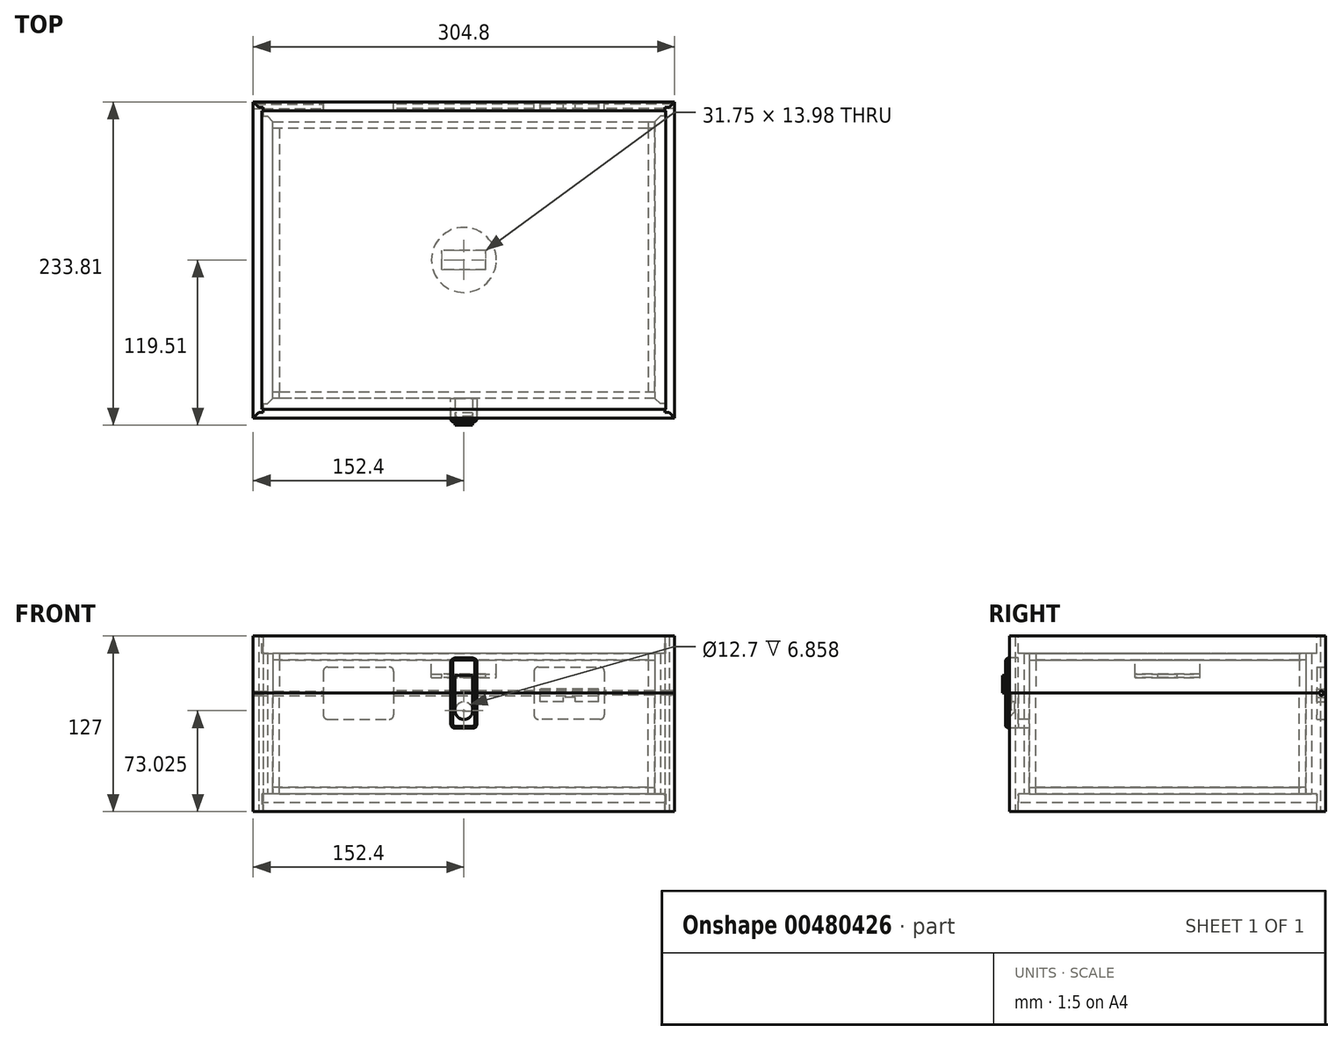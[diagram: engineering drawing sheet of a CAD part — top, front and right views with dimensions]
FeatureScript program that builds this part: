
annotation { "Feature Type Name" : "Feature", "Feature Type Description" : "" }
export const myFeature = defineFeature(function(context is Context, id is Id, definition is map)
    precondition{}
    {
        {
            var Q0;
            Q0=qCreatedBy(makeId("Top.planeOp"),FACE);
            var sketch = newSketch(context, id + "F0", { "sketchPlane" : qUnion([Q0])});
            skLineSegment(sketch, "E0.bottom", {"start": v(152.4, 114.3) * mm, "end": v(-152.4, 114.3) * mm});
            skLineSegment(sketch, "E0.top", {"start": v(152.4, -114.3) * mm, "end": v(-152.4, -114.3) * mm});
            skLineSegment(sketch, "E0.left", {"start": v(152.4, 114.3) * mm, "end": v(152.4, -114.3) * mm});
            skLineSegment(sketch, "E0.right", {"start": v(-152.4, 114.3) * mm, "end": v(-152.4, -114.3) * mm});
            skPoint(sketch, "E0.middle", {"position": v(0, 0) * mm});
            skPoint(sketch, "E1.endSnap0", {"position": v(0, 114.3) * mm});
            skPoint(sketch, "E2.endSnap0", {"position": v(0, -114.3) * mm});
            skPoint(sketch, "E3.endSnap0", {"position": v(-152.4, 0) * mm});
            skLineSegment(sketch, "E4", {"start": v(152.4, 114.3) * mm, "end": v(138.11, 100.01) * mm});
            skLineSegment(sketch, "E5", {"start": v(145.26, 107.16) * mm, "end": v(145.26, 103.98) * mm});
            skLineSegment(sketch, "E6", {"start": v(145.26, 103.98) * mm, "end": v(142.08, 103.98) * mm});
            skLineSegment(sketch, "E7", {"start": v(145.26, 107.16) * mm, "end": v(145.26, 110.33) * mm});
            skLineSegment(sketch, "E8", {"start": v(145.26, 110.33) * mm, "end": v(148.43, 110.33) * mm});
            skLineSegment(sketch, "E9", {"start": v(152.4, -114.3) * mm, "end": v(138.11, -100.01) * mm});
            skLineSegment(sketch, "E10", {"start": v(-152.4, -114.3) * mm, "end": v(-138.11, -100.01) * mm});
            skLineSegment(sketch, "E11", {"start": v(-152.4, 114.3) * mm, "end": v(-138.11, 100.01) * mm});
            skLineSegment(sketch, "E12", {"start": v(145.26, -107.16) * mm, "end": v(145.26, -103.98) * mm});
            skLineSegment(sketch, "E13", {"start": v(145.26, -103.98) * mm, "end": v(142.08, -103.98) * mm});
            skLineSegment(sketch, "E14", {"start": v(145.26, -107.16) * mm, "end": v(145.26, -110.33) * mm});
            skLineSegment(sketch, "E15", {"start": v(145.26, -110.33) * mm, "end": v(148.43, -110.33) * mm});
            skLineSegment(sketch, "E16", {"start": v(-145.26, -107.16) * mm, "end": v(-145.26, -103.98) * mm});
            skLineSegment(sketch, "E17", {"start": v(-145.26, -103.98) * mm, "end": v(-142.08, -103.98) * mm});
            skLineSegment(sketch, "E18", {"start": v(-145.26, -107.16) * mm, "end": v(-145.26, -110.33) * mm});
            skLineSegment(sketch, "E19", {"start": v(-145.26, -110.33) * mm, "end": v(-148.43, -110.33) * mm});
            skLineSegment(sketch, "E20", {"start": v(-145.26, 107.16) * mm, "end": v(-145.26, 103.98) * mm});
            skLineSegment(sketch, "E21", {"start": v(-145.26, 103.98) * mm, "end": v(-142.08, 103.98) * mm});
            skLineSegment(sketch, "E22", {"start": v(-145.26, 107.16) * mm, "end": v(-145.26, 110.33) * mm});
            skLineSegment(sketch, "E23", {"start": v(-145.26, 110.33) * mm, "end": v(-148.43, 110.33) * mm});
            skLineSegment(sketch, "E24", {"start": v(-138.11, 100.01) * mm, "end": v(138.11, 100.01) * mm});
            skLineSegment(sketch, "E25", {"start": v(138.11, 100.01) * mm, "end": v(138.11, -100.01) * mm});
            skLineSegment(sketch, "E26", {"start": v(138.11, -100.01) * mm, "end": v(-138.11, -100.01) * mm});
            skLineSegment(sketch, "E27", {"start": v(-138.11, -100.01) * mm, "end": v(-138.11, 100.01) * mm});
            skSolve(sketch);
        }
        {
            var Q0;
            {var subQ5=sQuery(id+"F0.wireOp",EDGE,"E0.bottom");Q0=makeQuery(id+"F0.imprint","IMPRINT",FACE,{"disambiguationData":[TD([[makeQuery(id+"F0.imprint","IMPRINT",EDGE,{"derivedFrom":subQ5}),1.0]])]});}
            var Q1;
            {var subQ5=sQuery(id+"F0.wireOp",EDGE,"E0.top");Q1=makeQuery(id+"F0.imprint","IMPRINT",FACE,{"disambiguationData":[TD([[makeQuery(id+"F0.imprint","IMPRINT",EDGE,{"derivedFrom":subQ5}),-1.0]])]});}
            var Q2;
            {var subQ0=sQuery(id+"F0.wireOp",EDGE,"E16");Q2=makeQuery(id+"F0.imprint","IMPRINT",FACE,{"disambiguationData":[TD([[makeQuery(id+"F0.imprint","IMPRINT",EDGE,{"derivedFrom":subQ0}),-1.0]])]});}
            var Q3;
            {var subQ0=sQuery(id+"F0.wireOp",EDGE,"E12");Q3=makeQuery(id+"F0.imprint","IMPRINT",FACE,{"disambiguationData":[TD([[makeQuery(id+"F0.imprint","IMPRINT",EDGE,{"derivedFrom":subQ0}),1.0]])]});}
            var Q4;
            {var subQ0=sQuery(id+"F0.wireOp",EDGE,"E5");Q4=makeQuery(id+"F0.imprint","IMPRINT",FACE,{"disambiguationData":[TD([[makeQuery(id+"F0.imprint","IMPRINT",EDGE,{"derivedFrom":subQ0}),-1.0]])]});}
            var Q5;
            {var subQ0=sQuery(id+"F0.wireOp",EDGE,"E20");Q5=makeQuery(id+"F0.imprint","IMPRINT",FACE,{"disambiguationData":[TD([[makeQuery(id+"F0.imprint","IMPRINT",EDGE,{"derivedFrom":subQ0}),1.0]])]});}
            extrude(context, id + "F1", {"entities" : qUnion([Q0, Q1, Q2, Q3, Q4, Q5]), "depth" : 85.72 * mm});
        }
        {
            var Q0;
            {var subQ1=sQuery(id+"F0.wireOp",EDGE,"E0.left");Q0=makeQuery(id+"F0.imprint","IMPRINT",FACE,{"disambiguationData":[TD([[makeQuery(id+"F0.imprint","IMPRINT",EDGE,{"derivedFrom":subQ1}),-1.0]])]});}
            var Q1;
            {var subQ6=sQuery(id+"F0.wireOp",EDGE,"E0.right");Q1=makeQuery(id+"F0.imprint","IMPRINT",FACE,{"disambiguationData":[TD([[makeQuery(id+"F0.imprint","IMPRINT",EDGE,{"derivedFrom":subQ6}),1.0]])]});}
            var Q2;
            {var subQ0=sQuery(id+"F0.wireOp",EDGE,"E22");Q2=makeQuery(id+"F0.imprint","IMPRINT",FACE,{"disambiguationData":[TD([[makeQuery(id+"F0.imprint","IMPRINT",EDGE,{"derivedFrom":subQ0}),1.0]])]});}
            var Q3;
            {var subQ0=sQuery(id+"F0.wireOp",EDGE,"E7");Q3=makeQuery(id+"F0.imprint","IMPRINT",FACE,{"disambiguationData":[TD([[makeQuery(id+"F0.imprint","IMPRINT",EDGE,{"derivedFrom":subQ0}),-1.0]])]});}
            var Q4;
            {var subQ0=sQuery(id+"F0.wireOp",EDGE,"E14");Q4=makeQuery(id+"F0.imprint","IMPRINT",FACE,{"disambiguationData":[TD([[makeQuery(id+"F0.imprint","IMPRINT",EDGE,{"derivedFrom":subQ0}),1.0]])]});}
            var Q5;
            {var subQ0=sQuery(id+"F0.wireOp",EDGE,"E18");Q5=makeQuery(id+"F0.imprint","IMPRINT",FACE,{"disambiguationData":[TD([[makeQuery(id+"F0.imprint","IMPRINT",EDGE,{"derivedFrom":subQ0}),-1.0]])]});}
            extrude(context, id + "F2", {"entities" : qUnion([Q0, Q1, Q2, Q3, Q4, Q5]), "depth" : 85.72 * mm});
        }
        {
            var Q0;
            Q0=makeQuery(id+"F1.opExtrude","CAP_FACE",FACE,{"disambiguationData":[OSD([sQuery(id+"F0.wireOp",EDGE,"E0.top"),sQuery(id+"F0.wireOp",EDGE,"E9"),sQuery(id+"F0.wireOp",EDGE,"E10"),sQuery(id+"F0.wireOp",EDGE,"E12"),sQuery(id+"F0.wireOp",EDGE,"E13"),sQuery(id+"F0.wireOp",EDGE,"E14"),sQuery(id+"F0.wireOp",EDGE,"E15"),sQuery(id+"F0.wireOp",EDGE,"E16"),sQuery(id+"F0.wireOp",EDGE,"E17"),sQuery(id+"F0.wireOp",EDGE,"E18"),sQuery(id+"F0.wireOp",EDGE,"E19"),sQuery(id+"F0.wireOp",EDGE,"E26")])],"isStart":true});
            var sketch = newSketch(context, id + "F3", { "sketchPlane" : qUnion([Q0])});
            skLineSegment(sketch, "E28.bottom", {"start": v(146.05, -107.95) * mm, "end": v(-146.05, -107.95) * mm});
            skLineSegment(sketch, "E28.top", {"start": v(146.05, 107.95) * mm, "end": v(-146.05, 107.95) * mm});
            skLineSegment(sketch, "E28.left", {"start": v(146.05, -107.95) * mm, "end": v(146.05, 107.95) * mm});
            skLineSegment(sketch, "E28.right", {"start": v(-146.05, -107.95) * mm, "end": v(-146.05, 107.95) * mm});
            skPoint(sketch, "E28.middle", {"position": v(0, 0) * mm});
            skLineSegment(sketch, "E29.bottom", {"start": v(138.11, 100.01) * mm, "end": v(-138.11, 100.01) * mm});
            skLineSegment(sketch, "E29.top", {"start": v(138.11, -100.01) * mm, "end": v(-138.11, -100.01) * mm});
            skLineSegment(sketch, "E29.left", {"start": v(138.11, 100.01) * mm, "end": v(138.11, -100.01) * mm});
            skLineSegment(sketch, "E29.right", {"start": v(-138.11, 100.01) * mm, "end": v(-138.11, -100.01) * mm});
            skSolve(sketch);
        }
        {
            var Q0;
            Q0 = qSketchRegion(id + "F3", true);
            extrude(context, id + "F4", {"entities" : qUnion([Q0]), "operationType" : NewBodyOperationType.REMOVE, "oppositeDirection" : true, "depth" : 12.7 * mm});
        }
        {
            var Q0;
            Q0=makeQuery(id+"F3.imprint","IMPRINT",FACE,{"disambiguationData":[TD([[makeQuery(id+"F3.imprint","IMPRINT",EDGE,{"derivedFrom":sQuery(id+"F3.wireOp",EDGE,"E29.bottom")}),-1.0]])]});
            var Q1;
            Q1=makeQuery(id+"F3.imprint","IMPRINT",FACE,{"disambiguationData":[TD([[makeQuery(id+"F3.imprint","IMPRINT",EDGE,{"derivedFrom":sQuery(id+"F3.wireOp",EDGE,"E28.bottom")}),-1.0]])]});
            var Q2;
            Q2=makeQuery(id+"F3.imprint","IMPRINT",FACE,{"disambiguationData":[TD([[makeQuery(id+"F3.imprint","IMPRINT",EDGE,{"derivedFrom":sQuery(id+"F3.wireOp",EDGE,"E29.bottom")}),1.0]])]});
            extrude(context, id + "F5", {"entities" : qUnion([Q0, Q1, Q2]), "oppositeDirection" : true, "depth" : 6.35 * mm});
        }
        {
            var Q0;
            Q0=makeQuery(id+"F5.opExtrude","SWEPT_BODY",BODY,{"disambiguationData":[OSD([sQuery(id+"F3.wireOp",EDGE,"E28.bottom"),sQuery(id+"F3.wireOp",EDGE,"E28.top"),sQuery(id+"F3.wireOp",EDGE,"E28.left"),sQuery(id+"F3.wireOp",EDGE,"E28.right")])]});
            var Q1;
            Q1=makeQuery(id+"F1.opExtrude","SWEPT_EDGE",EDGE,{"disambiguationData":[OSD([sQuery(id+"F0.wireOp",EDGE,"E0.bottom"),sQuery(id+"F0.wireOp",EDGE,"E0.right"),sQuery(id+"F0.wireOp",EDGE,"E11")])]});
            transform(context, id + "F6", {"entities" : qUnion([Q0]), "transformType" : TransformType.TRANSLATION_DISTANCE, "transformDirection" : qUnion([Q1]), "distance" : 6.35 * mm, "oppositeDirection" : true, "makeCopy" : false});
        }
        {
            var Q0;
            Q0=makeQuery(id+"F1.opExtrude","CAP_FACE",FACE,{"disambiguationData":[OSD([sQuery(id+"F0.wireOp",EDGE,"E0.bottom"),sQuery(id+"F0.wireOp",EDGE,"E4"),sQuery(id+"F0.wireOp",EDGE,"E5"),sQuery(id+"F0.wireOp",EDGE,"E6"),sQuery(id+"F0.wireOp",EDGE,"E7"),sQuery(id+"F0.wireOp",EDGE,"E8"),sQuery(id+"F0.wireOp",EDGE,"E11"),sQuery(id+"F0.wireOp",EDGE,"E20"),sQuery(id+"F0.wireOp",EDGE,"E21"),sQuery(id+"F0.wireOp",EDGE,"E22"),sQuery(id+"F0.wireOp",EDGE,"E23"),sQuery(id+"F0.wireOp",EDGE,"E24")])],"isStart":false});
            var Q1;
            Q1=makeQuery(id+"F2.opExtrude","CAP_FACE",FACE,{"disambiguationData":[OSD([sQuery(id+"F0.wireOp",EDGE,"E0.right"),sQuery(id+"F0.wireOp",EDGE,"E10"),sQuery(id+"F0.wireOp",EDGE,"E11"),sQuery(id+"F0.wireOp",EDGE,"E16"),sQuery(id+"F0.wireOp",EDGE,"E17"),sQuery(id+"F0.wireOp",EDGE,"E18"),sQuery(id+"F0.wireOp",EDGE,"E19"),sQuery(id+"F0.wireOp",EDGE,"E20"),sQuery(id+"F0.wireOp",EDGE,"E21"),sQuery(id+"F0.wireOp",EDGE,"E22"),sQuery(id+"F0.wireOp",EDGE,"E23"),sQuery(id+"F0.wireOp",EDGE,"E27")])],"isStart":false});
            var Q2;
            Q2=makeQuery(id+"F1.opExtrude","CAP_FACE",FACE,{"disambiguationData":[OSD([sQuery(id+"F0.wireOp",EDGE,"E0.top"),sQuery(id+"F0.wireOp",EDGE,"E9"),sQuery(id+"F0.wireOp",EDGE,"E10"),sQuery(id+"F0.wireOp",EDGE,"E12"),sQuery(id+"F0.wireOp",EDGE,"E13"),sQuery(id+"F0.wireOp",EDGE,"E14"),sQuery(id+"F0.wireOp",EDGE,"E15"),sQuery(id+"F0.wireOp",EDGE,"E16"),sQuery(id+"F0.wireOp",EDGE,"E17"),sQuery(id+"F0.wireOp",EDGE,"E18"),sQuery(id+"F0.wireOp",EDGE,"E19"),sQuery(id+"F0.wireOp",EDGE,"E26")])],"isStart":false});
            var Q3;
            Q3=makeQuery(id+"F2.opExtrude","CAP_FACE",FACE,{"disambiguationData":[OSD([sQuery(id+"F0.wireOp",EDGE,"E0.left"),sQuery(id+"F0.wireOp",EDGE,"E4"),sQuery(id+"F0.wireOp",EDGE,"E5"),sQuery(id+"F0.wireOp",EDGE,"E6"),sQuery(id+"F0.wireOp",EDGE,"E7"),sQuery(id+"F0.wireOp",EDGE,"E8"),sQuery(id+"F0.wireOp",EDGE,"E9"),sQuery(id+"F0.wireOp",EDGE,"E12"),sQuery(id+"F0.wireOp",EDGE,"E13"),sQuery(id+"F0.wireOp",EDGE,"E14"),sQuery(id+"F0.wireOp",EDGE,"E15"),sQuery(id+"F0.wireOp",EDGE,"E25")])],"isStart":false});
            extrude(context, id + "F7", {"entities" : qUnion([Q0, Q1, Q2, Q3]), "depth" : 41.27 * mm});
        }
        {
            var Q0;
            Q0=makeQuery(id+"F7.opExtrude","CAP_FACE",FACE,{"disambiguationData":[OSD([sQuery(id+"F0.wireOp",EDGE,"E0.left"),sQuery(id+"F0.wireOp",EDGE,"E4"),sQuery(id+"F0.wireOp",EDGE,"E5"),sQuery(id+"F0.wireOp",EDGE,"E6"),sQuery(id+"F0.wireOp",EDGE,"E7"),sQuery(id+"F0.wireOp",EDGE,"E8"),sQuery(id+"F0.wireOp",EDGE,"E9"),sQuery(id+"F0.wireOp",EDGE,"E12"),sQuery(id+"F0.wireOp",EDGE,"E13"),sQuery(id+"F0.wireOp",EDGE,"E14"),sQuery(id+"F0.wireOp",EDGE,"E15"),sQuery(id+"F0.wireOp",EDGE,"E25")])],"isStart":false});
            var sketch = newSketch(context, id + "F8", { "sketchPlane" : qUnion([Q0])});
            skLineSegment(sketch, "E30.bottom", {"start": v(146.05, 107.95) * mm, "end": v(-146.05, 107.95) * mm});
            skLineSegment(sketch, "E30.top", {"start": v(146.05, -107.95) * mm, "end": v(-146.05, -107.95) * mm});
            skLineSegment(sketch, "E30.left", {"start": v(146.05, 107.95) * mm, "end": v(146.05, -107.95) * mm});
            skLineSegment(sketch, "E30.right", {"start": v(-146.05, 107.95) * mm, "end": v(-146.05, -107.95) * mm});
            skPoint(sketch, "E30.middle", {"position": v(0, 0) * mm});
            skSolve(sketch);
        }
        {
            var Q0;
            Q0 = qSketchRegion(id + "F8", true);
            extrude(context, id + "F9", {"entities" : qUnion([Q0]), "operationType" : NewBodyOperationType.REMOVE, "oppositeDirection" : true, "depth" : 12.7 * mm});
        }
        {
            var Q0;
            Q0 = qSketchRegion(id + "F8", true);
            extrude(context, id + "F10", {"entities" : qUnion([Q0]), "oppositeDirection" : true, "depth" : 12.7 * mm});
        }
        {
            var Q0;
            Q0=makeQuery(id+"F1.opExtrude","CAP_FACE",FACE,{"disambiguationData":[OSD([sQuery(id+"F0.wireOp",EDGE,"E0.top"),sQuery(id+"F0.wireOp",EDGE,"E9"),sQuery(id+"F0.wireOp",EDGE,"E10"),sQuery(id+"F0.wireOp",EDGE,"E12"),sQuery(id+"F0.wireOp",EDGE,"E13"),sQuery(id+"F0.wireOp",EDGE,"E14"),sQuery(id+"F0.wireOp",EDGE,"E15"),sQuery(id+"F0.wireOp",EDGE,"E16"),sQuery(id+"F0.wireOp",EDGE,"E17"),sQuery(id+"F0.wireOp",EDGE,"E18"),sQuery(id+"F0.wireOp",EDGE,"E19"),sQuery(id+"F0.wireOp",EDGE,"E26")])],"isStart":false});
            var sketch = newSketch(context, id + "F11", { "sketchPlane" : qUnion([Q0])});
            skLineSegment(sketch, "E31.bottom", {"start": v(-138.11, -100.01) * mm, "end": v(138.11, -100.01) * mm});
            skLineSegment(sketch, "E31.top", {"start": v(-138.11, 100.01) * mm, "end": v(138.11, 100.01) * mm});
            skLineSegment(sketch, "E31.left", {"start": v(-138.11, -100.01) * mm, "end": v(-138.11, 100.01) * mm});
            skLineSegment(sketch, "E31.right", {"start": v(138.11, -100.01) * mm, "end": v(138.11, 100.01) * mm});
            skLineSegment(sketch, "E32.bottom", {"start": v(138.11, 100.01) * mm, "end": v(133.35, 100.01) * mm});
            skLineSegment(sketch, "E32.top", {"start": v(138.11, 95.25) * mm, "end": v(133.35, 95.25) * mm});
            skLineSegment(sketch, "E32.left", {"start": v(138.11, 100.01) * mm, "end": v(138.11, 95.25) * mm});
            skLineSegment(sketch, "E32.right", {"start": v(133.35, 100.01) * mm, "end": v(133.35, 95.25) * mm});
            skLineSegment(sketch, "E33.bottom", {"start": v(-138.11, -100.01) * mm, "end": v(-133.35, -100.01) * mm});
            skLineSegment(sketch, "E33.top", {"start": v(-138.11, -95.25) * mm, "end": v(-133.35, -95.25) * mm});
            skLineSegment(sketch, "E33.left", {"start": v(-138.11, -100.01) * mm, "end": v(-138.11, -95.25) * mm});
            skLineSegment(sketch, "E33.right", {"start": v(-133.35, -100.01) * mm, "end": v(-133.35, -95.25) * mm});
            skLineSegment(sketch, "E34.bottom", {"start": v(133.35, 95.25) * mm, "end": v(-133.35, 95.25) * mm});
            skLineSegment(sketch, "E34.top", {"start": v(133.35, -95.25) * mm, "end": v(-133.35, -95.25) * mm});
            skLineSegment(sketch, "E34.left", {"start": v(133.35, 95.25) * mm, "end": v(133.35, -95.25) * mm});
            skLineSegment(sketch, "E34.right", {"start": v(-133.35, 95.25) * mm, "end": v(-133.35, -95.25) * mm});
            skLineSegment(sketch, "E35", {"start": v(-133.35, 95.25) * mm, "end": v(-138.11, 95.25) * mm});
            skLineSegment(sketch, "E36", {"start": v(133.35, -95.25) * mm, "end": v(138.11, -95.25) * mm});
            skSolve(sketch);
        }
        {
            var Q0;
            Q0=makeQuery(id+"F11.imprint","IMPRINT",FACE,{"disambiguationData":[TD([[makeQuery(id+"F11.imprint","IMPRINT",EDGE,{"derivedFrom":sQuery(id+"F11.wireOp",EDGE,"E32.bottom")}),1.0]])]});
            var Q1;
            {var subQ1=sQuery(id+"F11.wireOp",EDGE,"E31.top");Q1=makeQuery(id+"F11.imprint","IMPRINT",FACE,{"disambiguationData":[TD([[makeQuery(id+"F11.imprint","IMPRINT",EDGE,{"derivedFrom":subQ1}),-1.0]])]});}
            var Q2;
            Q2=makeQuery(id+"F11.imprint","IMPRINT",FACE,{"disambiguationData":[TD([[makeQuery(id+"F11.imprint","IMPRINT",EDGE,{"derivedFrom":sQuery(id+"F11.wireOp",EDGE,"E33.bottom")}),-1.0]])]});
            var Q3;
            {var subQ1=sQuery(id+"F11.wireOp",EDGE,"E31.bottom");Q3=makeQuery(id+"F11.imprint","IMPRINT",FACE,{"disambiguationData":[TD([[makeQuery(id+"F11.imprint","IMPRINT",EDGE,{"derivedFrom":subQ1}),-1.0]])]});}
            extrude(context, id + "F12", {"entities" : qUnion([Q0, Q1, Q2, Q3]), "oppositeDirection" : true, "depth" : 68.26 * mm, "hasSecondDirection" : true, "secondDirectionOppositeDirection" : false, "secondDirectionDepth" : 3 / 406.4 * mm});
        }
        {
            var Q0;
            {var subQ0=sQuery(id+"F11.wireOp",EDGE,"E32.top");Q0=makeQuery(id+"F11.imprint","IMPRINT",FACE,{"disambiguationData":[TD([[makeQuery(id+"F11.imprint","IMPRINT",EDGE,{"derivedFrom":subQ0}),1.0]])]});}
            var Q1;
            {var subQ1=sQuery(id+"F11.wireOp",EDGE,"E31.bottom");Q1=makeQuery(id+"F11.imprint","IMPRINT",FACE,{"disambiguationData":[TD([[makeQuery(id+"F11.imprint","IMPRINT",EDGE,{"derivedFrom":subQ1}),-1.0]])]});}
            var Q2;
            Q2=makeQuery(id+"F11.imprint","IMPRINT",FACE,{"disambiguationData":[TD([[makeQuery(id+"F11.imprint","IMPRINT",EDGE,{"derivedFrom":sQuery(id+"F11.wireOp",EDGE,"E34.bottom")}),1.0]])]});
            var Q3;
            Q3=makeQuery(id+"F11.imprint","IMPRINT",FACE,{"disambiguationData":[TD([[makeQuery(id+"F11.imprint","IMPRINT",EDGE,{"derivedFrom":sQuery(id+"F11.wireOp",EDGE,"E32.bottom")}),1.0]])]});
            var Q4;
            {var subQ1=sQuery(id+"F11.wireOp",EDGE,"E31.top");Q4=makeQuery(id+"F11.imprint","IMPRINT",FACE,{"disambiguationData":[TD([[makeQuery(id+"F11.imprint","IMPRINT",EDGE,{"derivedFrom":subQ1}),-1.0]])]});}
            var Q5;
            Q5=makeQuery(id+"F11.imprint","IMPRINT",FACE,{"disambiguationData":[TD([[makeQuery(id+"F11.imprint","IMPRINT",EDGE,{"derivedFrom":sQuery(id+"F11.wireOp",EDGE,"E33.bottom")}),-1.0]])]});
            var Q6;
            {var subQ0=sQuery(id+"F11.wireOp",EDGE,"E33.top");Q6=makeQuery(id+"F11.imprint","IMPRINT",FACE,{"disambiguationData":[TD([[makeQuery(id+"F11.imprint","IMPRINT",EDGE,{"derivedFrom":subQ0}),1.0]])]});}
            extrude(context, id + "F13", {"entities" : qUnion([Q0, Q1, Q2, Q3, Q4, Q5, Q6]), "oppositeDirection" : true, "depth" : 73.02 * mm, "hasSecondDirection" : true, "secondDirectionOppositeDirection" : true, "secondDirectionDepth" : 68.26 * mm});
        }
        {
            var Q0;
            {var subQ0=sQuery(id+"F11.wireOp",EDGE,"E32.top");Q0=makeQuery(id+"F11.imprint","IMPRINT",FACE,{"disambiguationData":[TD([[makeQuery(id+"F11.imprint","IMPRINT",EDGE,{"derivedFrom":subQ0}),1.0]])]});}
            var Q1;
            {var subQ0=sQuery(id+"F11.wireOp",EDGE,"E33.top");Q1=makeQuery(id+"F11.imprint","IMPRINT",FACE,{"disambiguationData":[TD([[makeQuery(id+"F11.imprint","IMPRINT",EDGE,{"derivedFrom":subQ0}),1.0]])]});}
            extrude(context, id + "F14", {"entities" : qUnion([Q0, Q1]), "oppositeDirection" : true, "depth" : 68.26 * mm, "hasSecondDirection" : true, "secondDirectionOppositeDirection" : false, "secondDirectionDepth" : 3 / 406.4 * mm});
        }
        {
            var Q0;
            {var subQ1=sQuery(id+"F11.wireOp",EDGE,"E31.bottom");Q0=makeQuery(id+"F11.imprint","IMPRINT",FACE,{"disambiguationData":[TD([[makeQuery(id+"F11.imprint","IMPRINT",EDGE,{"derivedFrom":subQ1}),-1.0]])]});}
            var Q1;
            Q1=makeQuery(id+"F11.imprint","IMPRINT",FACE,{"disambiguationData":[TD([[makeQuery(id+"F11.imprint","IMPRINT",EDGE,{"derivedFrom":sQuery(id+"F11.wireOp",EDGE,"E33.bottom")}),-1.0]])]});
            var Q2;
            Q2=makeQuery(id+"F11.imprint","IMPRINT",FACE,{"disambiguationData":[TD([[makeQuery(id+"F11.imprint","IMPRINT",EDGE,{"derivedFrom":sQuery(id+"F11.wireOp",EDGE,"E32.bottom")}),1.0]])]});
            var Q3;
            {var subQ1=sQuery(id+"F11.wireOp",EDGE,"E31.top");Q3=makeQuery(id+"F11.imprint","IMPRINT",FACE,{"disambiguationData":[TD([[makeQuery(id+"F11.imprint","IMPRINT",EDGE,{"derivedFrom":subQ1}),-1.0]])]});}
            extrude(context, id + "F15", {"entities" : qUnion([Q0, Q1, Q2, Q3]), "depth" : 23.8 * mm, "hasSecondDirection" : true, "secondDirectionOppositeDirection" : false, "secondDirectionDepth" : 3 / 406.4 * mm});
        }
        {
            var Q0;
            {var subQ1=sQuery(id+"F11.wireOp",EDGE,"E31.bottom");Q0=makeQuery(id+"F11.imprint","IMPRINT",FACE,{"disambiguationData":[TD([[makeQuery(id+"F11.imprint","IMPRINT",EDGE,{"derivedFrom":subQ1}),-1.0]])]});}
            var Q1;
            {var subQ0=sQuery(id+"F11.wireOp",EDGE,"E32.top");Q1=makeQuery(id+"F11.imprint","IMPRINT",FACE,{"disambiguationData":[TD([[makeQuery(id+"F11.imprint","IMPRINT",EDGE,{"derivedFrom":subQ0}),1.0]])]});}
            var Q2;
            Q2=makeQuery(id+"F11.imprint","IMPRINT",FACE,{"disambiguationData":[TD([[makeQuery(id+"F11.imprint","IMPRINT",EDGE,{"derivedFrom":sQuery(id+"F11.wireOp",EDGE,"E34.bottom")}),1.0]])]});
            var Q3;
            Q3=makeQuery(id+"F11.imprint","IMPRINT",FACE,{"disambiguationData":[TD([[makeQuery(id+"F11.imprint","IMPRINT",EDGE,{"derivedFrom":sQuery(id+"F11.wireOp",EDGE,"E32.bottom")}),1.0]])]});
            var Q4;
            {var subQ1=sQuery(id+"F11.wireOp",EDGE,"E31.top");Q4=makeQuery(id+"F11.imprint","IMPRINT",FACE,{"disambiguationData":[TD([[makeQuery(id+"F11.imprint","IMPRINT",EDGE,{"derivedFrom":subQ1}),-1.0]])]});}
            var Q5;
            {var subQ0=sQuery(id+"F11.wireOp",EDGE,"E33.top");Q5=makeQuery(id+"F11.imprint","IMPRINT",FACE,{"disambiguationData":[TD([[makeQuery(id+"F11.imprint","IMPRINT",EDGE,{"derivedFrom":subQ0}),1.0]])]});}
            var Q6;
            Q6=makeQuery(id+"F11.imprint","IMPRINT",FACE,{"disambiguationData":[TD([[makeQuery(id+"F11.imprint","IMPRINT",EDGE,{"derivedFrom":sQuery(id+"F11.wireOp",EDGE,"E33.bottom")}),-1.0]])]});
            extrude(context, id + "F16", {"entities" : qUnion([Q0, Q1, Q2, Q3, Q4, Q5, Q6]), "depth" : 28.57 * mm, "hasSecondDirection" : true, "secondDirectionOppositeDirection" : false, "secondDirectionDepth" : 23.8 * mm});
        }
        {
            var Q0;
            {var subQ0=sQuery(id+"F11.wireOp",EDGE,"E33.top");Q0=makeQuery(id+"F11.imprint","IMPRINT",FACE,{"disambiguationData":[TD([[makeQuery(id+"F11.imprint","IMPRINT",EDGE,{"derivedFrom":subQ0}),1.0]])]});}
            var Q1;
            {var subQ0=sQuery(id+"F11.wireOp",EDGE,"E32.top");Q1=makeQuery(id+"F11.imprint","IMPRINT",FACE,{"disambiguationData":[TD([[makeQuery(id+"F11.imprint","IMPRINT",EDGE,{"derivedFrom":subQ0}),1.0]])]});}
            extrude(context, id + "F17", {"entities" : qUnion([Q0, Q1]), "depth" : 23.8 * mm, "hasSecondDirection" : true, "secondDirectionOppositeDirection" : false, "secondDirectionDepth" : 3 / 406.4 * mm});
        }
        {
            var Q0;
            Q0=makeQuery(id+"F1.opExtrude","SWEPT_FACE",FACE,{"disambiguationData":[OSD([sQuery(id+"F0.wireOp",EDGE,"E0.bottom")])]});
            var sketch = newSketch(context, id + "F18", { "sketchPlane" : qUnion([Q0])});
            skLineSegment(sketch, "E37", {"start": v(-152.4, 85.73) * mm, "end": v(-101.6, 85.73) * mm});
            skLineSegment(sketch, "E38", {"start": v(152.4, 85.73) * mm, "end": v(101.6, 85.73) * mm});
            skLineSegment(sketch, "E39.bottom", {"start": v(-101.6, 85.73) * mm, "end": v(-50.8, 85.73) * mm});
            skLineSegment(sketch, "E39.top", {"start": v(-101.6, 66.8) * mm, "end": v(-50.8, 66.8) * mm});
            skLineSegment(sketch, "E39.left", {"start": v(-101.6, 85.73) * mm, "end": v(-101.6, 66.8) * mm});
            skLineSegment(sketch, "E39.right", {"start": v(-50.8, 85.73) * mm, "end": v(-50.8, 66.8) * mm});
            skLineSegment(sketch, "E40.bottom", {"start": v(101.6, 85.73) * mm, "end": v(50.8, 85.73) * mm});
            skLineSegment(sketch, "E40.top", {"start": v(101.6, 66.8) * mm, "end": v(50.8, 66.8) * mm});
            skLineSegment(sketch, "E40.left", {"start": v(101.6, 85.73) * mm, "end": v(101.6, 66.8) * mm});
            skLineSegment(sketch, "E40.right", {"start": v(50.8, 85.73) * mm, "end": v(50.8, 66.8) * mm});
            skLineSegment(sketch, "E41.top", {"start": v(101.6, 104.65) * mm, "end": v(50.8, 104.65) * mm});
            skLineSegment(sketch, "E41.left", {"start": v(101.6, 85.73) * mm, "end": v(101.6, 104.65) * mm});
            skLineSegment(sketch, "E41.right", {"start": v(50.8, 85.73) * mm, "end": v(50.8, 104.65) * mm});
            skLineSegment(sketch, "E42.bottom", {"start": v(-50.8, 85.73) * mm, "end": v(-101.6, 85.73) * mm});
            skLineSegment(sketch, "E42.top", {"start": v(-50.8, 104.65) * mm, "end": v(-101.6, 104.65) * mm});
            skLineSegment(sketch, "E42.left", {"start": v(-50.8, 85.73) * mm, "end": v(-50.8, 104.65) * mm});
            skLineSegment(sketch, "E42.right", {"start": v(-101.6, 85.73) * mm, "end": v(-101.6, 104.65) * mm});
            skLineSegment(sketch, "E43", {"start": v(-101.6, 85.73) * mm, "end": v(-101.6, 79.38) * mm});
            skLineSegment(sketch, "E44.bottom", {"start": v(-101.6, 79.38) * mm, "end": v(-50.8, 79.38) * mm});
            skLineSegment(sketch, "E44.top", {"start": v(-101.6, 92.08) * mm, "end": v(-50.8, 92.08) * mm});
            skLineSegment(sketch, "E44.left", {"start": v(-101.6, 79.38) * mm, "end": v(-101.6, 92.08) * mm});
            skLineSegment(sketch, "E44.right", {"start": v(-50.8, 79.38) * mm, "end": v(-50.8, 92.08) * mm});
            skLineSegment(sketch, "E45", {"start": v(50.8, 85.73) * mm, "end": v(50.8, 79.38) * mm});
            skLineSegment(sketch, "E46.bottom", {"start": v(50.8, 79.38) * mm, "end": v(101.6, 79.38) * mm});
            skLineSegment(sketch, "E46.top", {"start": v(50.8, 92.08) * mm, "end": v(101.6, 92.08) * mm});
            skLineSegment(sketch, "E46.left", {"start": v(50.8, 79.38) * mm, "end": v(50.8, 92.08) * mm});
            skLineSegment(sketch, "E46.right", {"start": v(101.6, 79.38) * mm, "end": v(101.6, 92.08) * mm});
            skLineSegment(sketch, "E47", {"start": v(-50.8, 79.38) * mm, "end": v(-55.03, 79.38) * mm});
            skLineSegment(sketch, "E48", {"start": v(-55.03, 79.38) * mm, "end": v(-63.5, 79.38) * mm});
            skLineSegment(sketch, "E49", {"start": v(-63.5, 79.38) * mm, "end": v(-76.2, 79.38) * mm});
            skLineSegment(sketch, "E50", {"start": v(-63.5, 79.38) * mm, "end": v(-71.97, 79.38) * mm});
            skLineSegment(sketch, "E51", {"start": v(-71.97, 79.38) * mm, "end": v(-80.43, 79.38) * mm});
            skLineSegment(sketch, "E52", {"start": v(-80.43, 79.38) * mm, "end": v(-88.9, 79.38) * mm});
            skLineSegment(sketch, "E53", {"start": v(-88.9, 79.38) * mm, "end": v(-97.37, 79.38) * mm});
            skLineSegment(sketch, "E54", {"start": v(-97.37, 79.38) * mm, "end": v(-97.37, 92.08) * mm});
            skLineSegment(sketch, "E55", {"start": v(-88.9, 79.38) * mm, "end": v(-88.9, 92.08) * mm});
            skLineSegment(sketch, "E56", {"start": v(-80.43, 79.38) * mm, "end": v(-80.43, 92.08) * mm});
            skLineSegment(sketch, "E57", {"start": v(-71.97, 79.38) * mm, "end": v(-71.97, 92.08) * mm});
            skLineSegment(sketch, "E58", {"start": v(-55.03, 79.38) * mm, "end": v(-55.03, 92.08) * mm});
            skLineSegment(sketch, "E59", {"start": v(-63.5, 79.38) * mm, "end": v(-63.5, 92.08) * mm});
            skLineSegment(sketch, "E60", {"start": v(-101.6, 88.84) * mm, "end": v(-50.8, 88.84) * mm});
            skLineSegment(sketch, "E61", {"start": v(-101.6, 82.55) * mm, "end": v(-50.8, 82.55) * mm});
            skLineSegment(sketch, "E62", {"start": v(50.8, 85.73) * mm, "end": v(55.03, 85.73) * mm});
            skLineSegment(sketch, "E63", {"start": v(55.03, 85.73) * mm, "end": v(63.5, 85.73) * mm});
            skLineSegment(sketch, "E64", {"start": v(63.5, 85.73) * mm, "end": v(71.97, 85.73) * mm});
            skLineSegment(sketch, "E65", {"start": v(71.97, 85.73) * mm, "end": v(80.43, 85.73) * mm});
            skLineSegment(sketch, "E66", {"start": v(80.43, 85.73) * mm, "end": v(88.9, 85.73) * mm});
            skLineSegment(sketch, "E67", {"start": v(88.9, 85.73) * mm, "end": v(97.37, 85.73) * mm});
            skLineSegment(sketch, "E68", {"start": v(55.03, 79.38) * mm, "end": v(55.03, 92.08) * mm});
            skLineSegment(sketch, "E69", {"start": v(63.5, 79.38) * mm, "end": v(63.5, 92.08) * mm});
            skLineSegment(sketch, "E70", {"start": v(71.97, 79.38) * mm, "end": v(71.97, 92.08) * mm});
            skLineSegment(sketch, "E71", {"start": v(80.43, 79.38) * mm, "end": v(80.43, 92.08) * mm});
            skLineSegment(sketch, "E72", {"start": v(88.9, 79.38) * mm, "end": v(88.9, 92.08) * mm});
            skLineSegment(sketch, "E73", {"start": v(97.37, 79.38) * mm, "end": v(97.37, 92.08) * mm});
            skLineSegment(sketch, "E74", {"start": v(50.8, 82.55) * mm, "end": v(101.6, 82.55) * mm});
            skLineSegment(sketch, "E75", {"start": v(50.8, 85.73) * mm, "end": v(50.8, 92.08) * mm});
            skLineSegment(sketch, "E76", {"start": v(50.8, 88.9) * mm, "end": v(101.6, 88.9) * mm});
            skSolve(sketch);
        }
        {
            var Q0;
            Q0=makeQuery(id+"F18.imprint","IMPRINT",FACE,{"disambiguationData":[TD([[makeQuery(id+"F18.imprint","IMPRINT",EDGE,{"derivedFrom":sQuery(id+"F18.wireOp",EDGE,"E39.top")}),1.0]])]});
            var Q1;
            {var subQ0=sQuery(id+"F18.wireOp",EDGE,"E44.bottom");Q1=makeQuery(id+"F18.imprint","IMPRINT",FACE,{"disambiguationData":[TD([[makeQuery(id+"F18.imprint","IMPRINT",EDGE,{"derivedFrom":subQ0}),1.0]])]});}
            var Q2;
            {var subQ1=sQuery(id+"F18.wireOp",EDGE,"E42.bottom");var subQ3=sQuery(id+"F18.wireOp",EDGE,"E54");var subQ4=makeQuery(id+"F18.imprint","INTERSECT",VERTEX,{"derivedFrom":[subQ1,subQ3]});Q2=makeQuery(id+"F18.imprint","IMPRINT",FACE,{"disambiguationData":[TD([[makeQuery(id+"F18.imprint","IMPRINT",EDGE,{"disambiguationData":[TD([[subQ4,1.0]])],"derivedFrom":subQ3}),1.0]])]});}
            var Q3;
            {var subQ1=sQuery(id+"F18.wireOp",EDGE,"E42.bottom");var subQ3=sQuery(id+"F18.wireOp",EDGE,"E54");var subQ4=makeQuery(id+"F18.imprint","INTERSECT",VERTEX,{"derivedFrom":[subQ1,subQ3]});Q3=makeQuery(id+"F18.imprint","IMPRINT",FACE,{"disambiguationData":[TD([[makeQuery(id+"F18.imprint","IMPRINT",EDGE,{"disambiguationData":[TD([[subQ4,-1.0]])],"derivedFrom":subQ3}),1.0]])]});}
            var Q4;
            {var subQ0=sQuery(id+"F18.wireOp",EDGE,"E53");Q4=makeQuery(id+"F18.imprint","IMPRINT",FACE,{"disambiguationData":[TD([[makeQuery(id+"F18.imprint","IMPRINT",EDGE,{"derivedFrom":subQ0}),-1.0]])]});}
            var Q5;
            {var subQ0=sQuery(id+"F18.wireOp",EDGE,"E52");Q5=makeQuery(id+"F18.imprint","IMPRINT",FACE,{"disambiguationData":[TD([[makeQuery(id+"F18.imprint","IMPRINT",EDGE,{"derivedFrom":subQ0}),-1.0]])]});}
            var Q6;
            {var subQ0=sQuery(id+"F18.wireOp",EDGE,"E55");var subQ1=sQuery(id+"F18.wireOp",EDGE,"E42.bottom");var subQ2=makeQuery(id+"F18.imprint","INTERSECT",VERTEX,{"derivedFrom":[subQ1,subQ0]});Q6=makeQuery(id+"F18.imprint","IMPRINT",FACE,{"disambiguationData":[TD([[makeQuery(id+"F18.imprint","IMPRINT",EDGE,{"disambiguationData":[TD([[subQ2,-1.0]])],"derivedFrom":subQ1}),1.0]])]});}
            var Q7;
            {var subQ0=sQuery(id+"F18.wireOp",EDGE,"E55");var subQ1=sQuery(id+"F18.wireOp",EDGE,"E42.bottom");var subQ2=makeQuery(id+"F18.imprint","INTERSECT",VERTEX,{"derivedFrom":[subQ1,subQ0]});Q7=makeQuery(id+"F18.imprint","IMPRINT",FACE,{"disambiguationData":[TD([[makeQuery(id+"F18.imprint","IMPRINT",EDGE,{"disambiguationData":[TD([[subQ2,-1.0]])],"derivedFrom":subQ1}),-1.0]])]});}
            var Q8;
            {var subQ1=sQuery(id+"F18.wireOp",EDGE,"E51");var subQ5=makeQuery(id+"F18.imprint","IMPRINT",VERTEX,{"derivedFrom":subQ1});Q8=makeQuery(id+"F18.imprint","IMPRINT",FACE,{"disambiguationData":[TD([[makeQuery(id+"F18.imprint","IMPRINT",EDGE,{"disambiguationData":[TD([[subQ5,1.0]])],"derivedFrom":subQ1}),-1.0]])]});}
            var Q9;
            {var subQ0=sQuery(id+"F18.wireOp",EDGE,"E50");Q9=makeQuery(id+"F18.imprint","IMPRINT",FACE,{"disambiguationData":[TD([[makeQuery(id+"F18.imprint","IMPRINT",EDGE,{"derivedFrom":subQ0}),-1.0]])]});}
            var Q10;
            {var subQ0=sQuery(id+"F18.wireOp",EDGE,"E48");Q10=makeQuery(id+"F18.imprint","IMPRINT",FACE,{"disambiguationData":[TD([[makeQuery(id+"F18.imprint","IMPRINT",EDGE,{"derivedFrom":subQ0}),-1.0]])]});}
            var Q11;
            {var subQ0=sQuery(id+"F18.wireOp",EDGE,"E57");var subQ1=sQuery(id+"F18.wireOp",EDGE,"E42.bottom");var subQ2=makeQuery(id+"F18.imprint","INTERSECT",VERTEX,{"derivedFrom":[subQ1,subQ0]});Q11=makeQuery(id+"F18.imprint","IMPRINT",FACE,{"disambiguationData":[TD([[makeQuery(id+"F18.imprint","IMPRINT",EDGE,{"disambiguationData":[TD([[subQ2,-1.0]])],"derivedFrom":subQ1}),-1.0]])]});}
            var Q12;
            {var subQ0=sQuery(id+"F18.wireOp",EDGE,"E57");var subQ1=sQuery(id+"F18.wireOp",EDGE,"E42.bottom");var subQ2=makeQuery(id+"F18.imprint","INTERSECT",VERTEX,{"derivedFrom":[subQ1,subQ0]});Q12=makeQuery(id+"F18.imprint","IMPRINT",FACE,{"disambiguationData":[TD([[makeQuery(id+"F18.imprint","IMPRINT",EDGE,{"disambiguationData":[TD([[subQ2,-1.0]])],"derivedFrom":subQ1}),1.0]])]});}
            var Q13;
            {var subQ0=sQuery(id+"F18.wireOp",EDGE,"E47");Q13=makeQuery(id+"F18.imprint","IMPRINT",FACE,{"disambiguationData":[TD([[makeQuery(id+"F18.imprint","IMPRINT",EDGE,{"derivedFrom":subQ0}),-1.0]])]});}
            var Q14;
            {var subQ1=sQuery(id+"F18.wireOp",EDGE,"E42.bottom");var subQ3=sQuery(id+"F18.wireOp",EDGE,"E58");var subQ4=makeQuery(id+"F18.imprint","INTERSECT",VERTEX,{"derivedFrom":[subQ1,subQ3]});Q14=makeQuery(id+"F18.imprint","IMPRINT",FACE,{"disambiguationData":[TD([[makeQuery(id+"F18.imprint","IMPRINT",EDGE,{"disambiguationData":[TD([[subQ4,1.0]])],"derivedFrom":subQ3}),-1.0]])]});}
            var Q15;
            {var subQ1=sQuery(id+"F18.wireOp",EDGE,"E42.bottom");var subQ3=sQuery(id+"F18.wireOp",EDGE,"E58");var subQ4=makeQuery(id+"F18.imprint","INTERSECT",VERTEX,{"derivedFrom":[subQ1,subQ3]});Q15=makeQuery(id+"F18.imprint","IMPRINT",FACE,{"disambiguationData":[TD([[makeQuery(id+"F18.imprint","IMPRINT",EDGE,{"disambiguationData":[TD([[subQ4,-1.0]])],"derivedFrom":subQ3}),-1.0]])]});}
            var Q16;
            {var subQ1=sQuery(id+"F18.wireOp",EDGE,"E46.bottom");var subQ3=sQuery(id+"F18.wireOp",EDGE,"E73");var subQ4=makeQuery(id+"F18.imprint","INTERSECT",VERTEX,{"derivedFrom":[subQ1,subQ3]});Q16=makeQuery(id+"F18.imprint","IMPRINT",FACE,{"disambiguationData":[TD([[makeQuery(id+"F18.imprint","IMPRINT",EDGE,{"disambiguationData":[TD([[subQ4,-1.0]])],"derivedFrom":subQ3}),-1.0]])]});}
            var Q17;
            {var subQ0=sQuery(id+"F18.wireOp",EDGE,"E40.bottom");Q17=makeQuery(id+"F18.imprint","IMPRINT",FACE,{"disambiguationData":[TD([[makeQuery(id+"F18.imprint","IMPRINT",EDGE,{"derivedFrom":subQ0}),-1.0]])]});}
            var Q18;
            {var subQ0=sQuery(id+"F18.wireOp",EDGE,"E40.bottom");Q18=makeQuery(id+"F18.imprint","IMPRINT",FACE,{"disambiguationData":[TD([[makeQuery(id+"F18.imprint","IMPRINT",EDGE,{"derivedFrom":subQ0}),1.0]])]});}
            var Q19;
            {var subQ0=sQuery(id+"F18.wireOp",EDGE,"E62");Q19=makeQuery(id+"F18.imprint","IMPRINT",FACE,{"disambiguationData":[TD([[makeQuery(id+"F18.imprint","IMPRINT",EDGE,{"derivedFrom":subQ0}),1.0]])]});}
            var Q20;
            {var subQ0=sQuery(id+"F18.wireOp",EDGE,"E62");Q20=makeQuery(id+"F18.imprint","IMPRINT",FACE,{"disambiguationData":[TD([[makeQuery(id+"F18.imprint","IMPRINT",EDGE,{"derivedFrom":subQ0}),-1.0]])]});}
            var Q21;
            {var subQ1=sQuery(id+"F18.wireOp",EDGE,"E46.bottom");var subQ3=sQuery(id+"F18.wireOp",EDGE,"E68");var subQ4=makeQuery(id+"F18.imprint","INTERSECT",VERTEX,{"derivedFrom":[subQ1,subQ3]});Q21=makeQuery(id+"F18.imprint","IMPRINT",FACE,{"disambiguationData":[TD([[makeQuery(id+"F18.imprint","IMPRINT",EDGE,{"disambiguationData":[TD([[subQ4,-1.0]])],"derivedFrom":subQ3}),1.0]])]});}
            var Q22;
            {var subQ0=sQuery(id+"F18.wireOp",EDGE,"E68");var subQ1=sQuery(id+"F18.wireOp",EDGE,"E46.bottom");var subQ2=makeQuery(id+"F18.imprint","INTERSECT",VERTEX,{"derivedFrom":[subQ1,subQ0]});Q22=makeQuery(id+"F18.imprint","IMPRINT",FACE,{"disambiguationData":[TD([[makeQuery(id+"F18.imprint","IMPRINT",EDGE,{"disambiguationData":[TD([[subQ2,-1.0]])],"derivedFrom":subQ1}),1.0]])]});}
            var Q23;
            {var subQ0=sQuery(id+"F18.wireOp",EDGE,"E64");Q23=makeQuery(id+"F18.imprint","IMPRINT",FACE,{"disambiguationData":[TD([[makeQuery(id+"F18.imprint","IMPRINT",EDGE,{"derivedFrom":subQ0}),1.0]])]});}
            var Q24;
            Q24=makeQuery(id+"F18.imprint","IMPRINT",FACE,{"disambiguationData":[TD([[makeQuery(id+"F18.imprint","IMPRINT",EDGE,{"derivedFrom":sQuery(id+"F18.wireOp",EDGE,"E40.top")}),-1.0]])]});
            var Q25;
            {var subQ0=sQuery(id+"F18.wireOp",EDGE,"E69");var subQ1=sQuery(id+"F18.wireOp",EDGE,"E46.bottom");var subQ2=makeQuery(id+"F18.imprint","INTERSECT",VERTEX,{"derivedFrom":[subQ1,subQ0]});Q25=makeQuery(id+"F18.imprint","IMPRINT",FACE,{"disambiguationData":[TD([[makeQuery(id+"F18.imprint","IMPRINT",EDGE,{"disambiguationData":[TD([[subQ2,-1.0]])],"derivedFrom":subQ1}),1.0]])]});}
            var Q26;
            {var subQ0=sQuery(id+"F18.wireOp",EDGE,"E64");Q26=makeQuery(id+"F18.imprint","IMPRINT",FACE,{"disambiguationData":[TD([[makeQuery(id+"F18.imprint","IMPRINT",EDGE,{"derivedFrom":subQ0}),-1.0]])]});}
            var Q27;
            {var subQ0=sQuery(id+"F18.wireOp",EDGE,"E70");var subQ1=sQuery(id+"F18.wireOp",EDGE,"E46.bottom");var subQ2=makeQuery(id+"F18.imprint","INTERSECT",VERTEX,{"derivedFrom":[subQ1,subQ0]});Q27=makeQuery(id+"F18.imprint","IMPRINT",FACE,{"disambiguationData":[TD([[makeQuery(id+"F18.imprint","IMPRINT",EDGE,{"disambiguationData":[TD([[subQ2,-1.0]])],"derivedFrom":subQ1}),1.0]])]});}
            var Q28;
            {var subQ0=sQuery(id+"F18.wireOp",EDGE,"E71");var subQ1=sQuery(id+"F18.wireOp",EDGE,"E46.bottom");var subQ2=makeQuery(id+"F18.imprint","INTERSECT",VERTEX,{"derivedFrom":[subQ1,subQ0]});Q28=makeQuery(id+"F18.imprint","IMPRINT",FACE,{"disambiguationData":[TD([[makeQuery(id+"F18.imprint","IMPRINT",EDGE,{"disambiguationData":[TD([[subQ2,-1.0]])],"derivedFrom":subQ1}),1.0]])]});}
            var Q29;
            {var subQ0=sQuery(id+"F18.wireOp",EDGE,"E66");Q29=makeQuery(id+"F18.imprint","IMPRINT",FACE,{"disambiguationData":[TD([[makeQuery(id+"F18.imprint","IMPRINT",EDGE,{"derivedFrom":subQ0}),-1.0]])]});}
            var Q30;
            {var subQ0=sQuery(id+"F18.wireOp",EDGE,"E66");Q30=makeQuery(id+"F18.imprint","IMPRINT",FACE,{"disambiguationData":[TD([[makeQuery(id+"F18.imprint","IMPRINT",EDGE,{"derivedFrom":subQ0}),1.0]])]});}
            var Q31;
            {var subQ0=sQuery(id+"F18.wireOp",EDGE,"E72");var subQ1=sQuery(id+"F18.wireOp",EDGE,"E46.bottom");var subQ2=makeQuery(id+"F18.imprint","INTERSECT",VERTEX,{"derivedFrom":[subQ1,subQ0]});Q31=makeQuery(id+"F18.imprint","IMPRINT",FACE,{"disambiguationData":[TD([[makeQuery(id+"F18.imprint","IMPRINT",EDGE,{"disambiguationData":[TD([[subQ2,-1.0]])],"derivedFrom":subQ1}),1.0]])]});}
            extrude(context, id + "F19", {"entities" : qUnion([Q0, Q1, Q2, Q3, Q4, Q5, Q6, Q7, Q8, Q9, Q10, Q11, Q12, Q13, Q14, Q15, Q16, Q17, Q18, Q19, Q20, Q21, Q22, Q23, Q24, Q25, Q26, Q27, Q28, Q29, Q30, Q31]), "oppositeDirection" : true, "depth" : 6.35 * mm});
        }
        {
            var Q0;
            {var subQ1=sQuery(id+"F18.wireOp",EDGE,"E46.top");var subQ3=sQuery(id+"F18.wireOp",EDGE,"E68");var subQ4=makeQuery(id+"F18.imprint","INTERSECT",VERTEX,{"derivedFrom":[subQ1,subQ3]});Q0=makeQuery(id+"F18.imprint","IMPRINT",FACE,{"disambiguationData":[TD([[makeQuery(id+"F18.imprint","IMPRINT",EDGE,{"disambiguationData":[TD([[subQ4,1.0]])],"derivedFrom":subQ3}),1.0]])]});}
            var Q1;
            {var subQ0=sQuery(id+"F18.wireOp",EDGE,"E63");Q1=makeQuery(id+"F18.imprint","IMPRINT",FACE,{"disambiguationData":[TD([[makeQuery(id+"F18.imprint","IMPRINT",EDGE,{"derivedFrom":subQ0}),-1.0]])]});}
            var Q2;
            {var subQ0=sQuery(id+"F18.wireOp",EDGE,"E63");Q2=makeQuery(id+"F18.imprint","IMPRINT",FACE,{"disambiguationData":[TD([[makeQuery(id+"F18.imprint","IMPRINT",EDGE,{"derivedFrom":subQ0}),1.0]])]});}
            var Q3;
            {var subQ0=sQuery(id+"F18.wireOp",EDGE,"E68");var subQ1=sQuery(id+"F18.wireOp",EDGE,"E46.top");var subQ2=makeQuery(id+"F18.imprint","INTERSECT",VERTEX,{"derivedFrom":[subQ1,subQ0]});Q3=makeQuery(id+"F18.imprint","IMPRINT",FACE,{"disambiguationData":[TD([[makeQuery(id+"F18.imprint","IMPRINT",EDGE,{"disambiguationData":[TD([[subQ2,-1.0]])],"derivedFrom":subQ1}),-1.0]])]});}
            var Q4;
            {var subQ4=sQuery(id+"F18.wireOp",EDGE,"E41.top");Q4=makeQuery(id+"F18.imprint","IMPRINT",FACE,{"disambiguationData":[TD([[makeQuery(id+"F18.imprint","IMPRINT",EDGE,{"derivedFrom":subQ4}),1.0]])]});}
            var Q5;
            {var subQ0=sQuery(id+"F18.wireOp",EDGE,"E69");var subQ1=sQuery(id+"F18.wireOp",EDGE,"E46.top");var subQ2=makeQuery(id+"F18.imprint","INTERSECT",VERTEX,{"derivedFrom":[subQ1,subQ0]});Q5=makeQuery(id+"F18.imprint","IMPRINT",FACE,{"disambiguationData":[TD([[makeQuery(id+"F18.imprint","IMPRINT",EDGE,{"disambiguationData":[TD([[subQ2,-1.0]])],"derivedFrom":subQ1}),-1.0]])]});}
            var Q6;
            {var subQ0=sQuery(id+"F18.wireOp",EDGE,"E70");var subQ1=sQuery(id+"F18.wireOp",EDGE,"E46.top");var subQ2=makeQuery(id+"F18.imprint","INTERSECT",VERTEX,{"derivedFrom":[subQ1,subQ0]});Q6=makeQuery(id+"F18.imprint","IMPRINT",FACE,{"disambiguationData":[TD([[makeQuery(id+"F18.imprint","IMPRINT",EDGE,{"disambiguationData":[TD([[subQ2,-1.0]])],"derivedFrom":subQ1}),-1.0]])]});}
            var Q7;
            {var subQ0=sQuery(id+"F18.wireOp",EDGE,"E65");Q7=makeQuery(id+"F18.imprint","IMPRINT",FACE,{"disambiguationData":[TD([[makeQuery(id+"F18.imprint","IMPRINT",EDGE,{"derivedFrom":subQ0}),1.0]])]});}
            var Q8;
            {var subQ0=sQuery(id+"F18.wireOp",EDGE,"E65");Q8=makeQuery(id+"F18.imprint","IMPRINT",FACE,{"disambiguationData":[TD([[makeQuery(id+"F18.imprint","IMPRINT",EDGE,{"derivedFrom":subQ0}),-1.0]])]});}
            var Q9;
            {var subQ0=sQuery(id+"F18.wireOp",EDGE,"E71");var subQ1=sQuery(id+"F18.wireOp",EDGE,"E46.top");var subQ2=makeQuery(id+"F18.imprint","INTERSECT",VERTEX,{"derivedFrom":[subQ1,subQ0]});Q9=makeQuery(id+"F18.imprint","IMPRINT",FACE,{"disambiguationData":[TD([[makeQuery(id+"F18.imprint","IMPRINT",EDGE,{"disambiguationData":[TD([[subQ2,-1.0]])],"derivedFrom":subQ1}),-1.0]])]});}
            var Q10;
            {var subQ0=sQuery(id+"F18.wireOp",EDGE,"E72");var subQ1=sQuery(id+"F18.wireOp",EDGE,"E46.top");var subQ2=makeQuery(id+"F18.imprint","INTERSECT",VERTEX,{"derivedFrom":[subQ1,subQ0]});Q10=makeQuery(id+"F18.imprint","IMPRINT",FACE,{"disambiguationData":[TD([[makeQuery(id+"F18.imprint","IMPRINT",EDGE,{"disambiguationData":[TD([[subQ2,-1.0]])],"derivedFrom":subQ1}),-1.0]])]});}
            var Q11;
            {var subQ1=sQuery(id+"F18.wireOp",EDGE,"E46.top");var subQ3=sQuery(id+"F18.wireOp",EDGE,"E73");var subQ4=makeQuery(id+"F18.imprint","INTERSECT",VERTEX,{"derivedFrom":[subQ1,subQ3]});Q11=makeQuery(id+"F18.imprint","IMPRINT",FACE,{"disambiguationData":[TD([[makeQuery(id+"F18.imprint","IMPRINT",EDGE,{"disambiguationData":[TD([[subQ4,1.0]])],"derivedFrom":subQ3}),-1.0]])]});}
            var Q12;
            {var subQ0=sQuery(id+"F18.wireOp",EDGE,"E67");Q12=makeQuery(id+"F18.imprint","IMPRINT",FACE,{"disambiguationData":[TD([[makeQuery(id+"F18.imprint","IMPRINT",EDGE,{"derivedFrom":subQ0}),-1.0]])]});}
            var Q13;
            {var subQ0=sQuery(id+"F18.wireOp",EDGE,"E67");Q13=makeQuery(id+"F18.imprint","IMPRINT",FACE,{"disambiguationData":[TD([[makeQuery(id+"F18.imprint","IMPRINT",EDGE,{"derivedFrom":subQ0}),1.0]])]});}
            var Q14;
            {var subQ0=sQuery(id+"F18.wireOp",EDGE,"E59");var subQ1=sQuery(id+"F18.wireOp",EDGE,"E42.bottom");var subQ2=makeQuery(id+"F18.imprint","INTERSECT",VERTEX,{"derivedFrom":[subQ1,subQ0]});Q14=makeQuery(id+"F18.imprint","IMPRINT",FACE,{"disambiguationData":[TD([[makeQuery(id+"F18.imprint","IMPRINT",EDGE,{"disambiguationData":[TD([[subQ2,-1.0]])],"derivedFrom":subQ1}),-1.0]])]});}
            var Q15;
            {var subQ0=sQuery(id+"F18.wireOp",EDGE,"E59");var subQ1=sQuery(id+"F18.wireOp",EDGE,"E42.bottom");var subQ2=makeQuery(id+"F18.imprint","INTERSECT",VERTEX,{"derivedFrom":[subQ1,subQ0]});Q15=makeQuery(id+"F18.imprint","IMPRINT",FACE,{"disambiguationData":[TD([[makeQuery(id+"F18.imprint","IMPRINT",EDGE,{"disambiguationData":[TD([[subQ2,-1.0]])],"derivedFrom":subQ1}),1.0]])]});}
            var Q16;
            {var subQ0=sQuery(id+"F18.wireOp",EDGE,"E56");var subQ1=sQuery(id+"F18.wireOp",EDGE,"E42.bottom");var subQ2=makeQuery(id+"F18.imprint","INTERSECT",VERTEX,{"derivedFrom":[subQ1,subQ0]});Q16=makeQuery(id+"F18.imprint","IMPRINT",FACE,{"disambiguationData":[TD([[makeQuery(id+"F18.imprint","IMPRINT",EDGE,{"disambiguationData":[TD([[subQ2,-1.0]])],"derivedFrom":subQ1}),1.0]])]});}
            var Q17;
            {var subQ0=sQuery(id+"F18.wireOp",EDGE,"E56");var subQ1=sQuery(id+"F18.wireOp",EDGE,"E42.bottom");var subQ2=makeQuery(id+"F18.imprint","INTERSECT",VERTEX,{"derivedFrom":[subQ1,subQ0]});Q17=makeQuery(id+"F18.imprint","IMPRINT",FACE,{"disambiguationData":[TD([[makeQuery(id+"F18.imprint","IMPRINT",EDGE,{"disambiguationData":[TD([[subQ2,-1.0]])],"derivedFrom":subQ1}),-1.0]])]});}
            var Q18;
            {var subQ0=sQuery(id+"F18.wireOp",EDGE,"E54");var subQ1=sQuery(id+"F18.wireOp",EDGE,"E42.bottom");var subQ2=makeQuery(id+"F18.imprint","INTERSECT",VERTEX,{"derivedFrom":[subQ1,subQ0]});Q18=makeQuery(id+"F18.imprint","IMPRINT",FACE,{"disambiguationData":[TD([[makeQuery(id+"F18.imprint","IMPRINT",EDGE,{"disambiguationData":[TD([[subQ2,-1.0]])],"derivedFrom":subQ1}),1.0]])]});}
            var Q19;
            {var subQ0=sQuery(id+"F18.wireOp",EDGE,"E54");var subQ1=sQuery(id+"F18.wireOp",EDGE,"E42.bottom");var subQ2=makeQuery(id+"F18.imprint","INTERSECT",VERTEX,{"derivedFrom":[subQ1,subQ0]});Q19=makeQuery(id+"F18.imprint","IMPRINT",FACE,{"disambiguationData":[TD([[makeQuery(id+"F18.imprint","IMPRINT",EDGE,{"disambiguationData":[TD([[subQ2,-1.0]])],"derivedFrom":subQ1}),-1.0]])]});}
            var Q20;
            {var subQ0=sQuery(id+"F18.wireOp",EDGE,"E54");var subQ1=sQuery(id+"F18.wireOp",EDGE,"E44.top");var subQ2=makeQuery(id+"F18.imprint","INTERSECT",VERTEX,{"derivedFrom":[subQ1,subQ0]});Q20=makeQuery(id+"F18.imprint","IMPRINT",FACE,{"disambiguationData":[TD([[makeQuery(id+"F18.imprint","IMPRINT",EDGE,{"disambiguationData":[TD([[subQ2,-1.0]])],"derivedFrom":subQ1}),-1.0]])]});}
            var Q21;
            {var subQ1=sQuery(id+"F18.wireOp",EDGE,"E44.top");var subQ3=sQuery(id+"F18.wireOp",EDGE,"E54");var subQ4=makeQuery(id+"F18.imprint","INTERSECT",VERTEX,{"derivedFrom":[subQ1,subQ3]});Q21=makeQuery(id+"F18.imprint","IMPRINT",FACE,{"disambiguationData":[TD([[makeQuery(id+"F18.imprint","IMPRINT",EDGE,{"disambiguationData":[TD([[subQ4,1.0]])],"derivedFrom":subQ3}),1.0]])]});}
            var Q22;
            {var subQ0=sQuery(id+"F18.wireOp",EDGE,"E55");var subQ1=sQuery(id+"F18.wireOp",EDGE,"E44.top");var subQ2=makeQuery(id+"F18.imprint","INTERSECT",VERTEX,{"derivedFrom":[subQ1,subQ0]});Q22=makeQuery(id+"F18.imprint","IMPRINT",FACE,{"disambiguationData":[TD([[makeQuery(id+"F18.imprint","IMPRINT",EDGE,{"disambiguationData":[TD([[subQ2,-1.0]])],"derivedFrom":subQ1}),-1.0]])]});}
            var Q23;
            {var subQ0=sQuery(id+"F18.wireOp",EDGE,"E56");var subQ1=sQuery(id+"F18.wireOp",EDGE,"E44.top");var subQ2=makeQuery(id+"F18.imprint","INTERSECT",VERTEX,{"derivedFrom":[subQ1,subQ0]});Q23=makeQuery(id+"F18.imprint","IMPRINT",FACE,{"disambiguationData":[TD([[makeQuery(id+"F18.imprint","IMPRINT",EDGE,{"disambiguationData":[TD([[subQ2,-1.0]])],"derivedFrom":subQ1}),-1.0]])]});}
            var Q24;
            {var subQ1=sQuery(id+"F18.wireOp",EDGE,"E44.top");var subQ3=sQuery(id+"F18.wireOp",EDGE,"E58");var subQ4=makeQuery(id+"F18.imprint","INTERSECT",VERTEX,{"derivedFrom":[subQ1,subQ3]});Q24=makeQuery(id+"F18.imprint","IMPRINT",FACE,{"disambiguationData":[TD([[makeQuery(id+"F18.imprint","IMPRINT",EDGE,{"disambiguationData":[TD([[subQ4,1.0]])],"derivedFrom":subQ3}),-1.0]])]});}
            var Q25;
            {var subQ0=sQuery(id+"F18.wireOp",EDGE,"E57");var subQ1=sQuery(id+"F18.wireOp",EDGE,"E44.top");var subQ2=makeQuery(id+"F18.imprint","INTERSECT",VERTEX,{"derivedFrom":[subQ1,subQ0]});Q25=makeQuery(id+"F18.imprint","IMPRINT",FACE,{"disambiguationData":[TD([[makeQuery(id+"F18.imprint","IMPRINT",EDGE,{"disambiguationData":[TD([[subQ2,-1.0]])],"derivedFrom":subQ1}),-1.0]])]});}
            var Q26;
            {var subQ0=sQuery(id+"F18.wireOp",EDGE,"E58");var subQ1=sQuery(id+"F18.wireOp",EDGE,"E44.top");var subQ2=makeQuery(id+"F18.imprint","INTERSECT",VERTEX,{"derivedFrom":[subQ1,subQ0]});Q26=makeQuery(id+"F18.imprint","IMPRINT",FACE,{"disambiguationData":[TD([[makeQuery(id+"F18.imprint","IMPRINT",EDGE,{"disambiguationData":[TD([[subQ2,1.0]])],"derivedFrom":subQ1}),-1.0]])]});}
            var Q27;
            {var subQ4=sQuery(id+"F18.wireOp",EDGE,"E42.top");Q27=makeQuery(id+"F18.imprint","IMPRINT",FACE,{"disambiguationData":[TD([[makeQuery(id+"F18.imprint","IMPRINT",EDGE,{"derivedFrom":subQ4}),1.0]])]});}
            extrude(context, id + "F20", {"entities" : qUnion([Q0, Q1, Q2, Q3, Q4, Q5, Q6, Q7, Q8, Q9, Q10, Q11, Q12, Q13, Q14, Q15, Q16, Q17, Q18, Q19, Q20, Q21, Q22, Q23, Q24, Q25, Q26, Q27]), "oppositeDirection" : true, "depth" : 6.35 * mm});
        }
        {
            var Q0;
            {var subQ0=sQuery(id+"F18.wireOp",EDGE,"E61");Q0=makeQuery(id+"F20.opExtrude","CAP_EDGE",EDGE,{"disambiguationData":[OSD([subQ0]),TDD([makeQuery(id+"F18.imprint","IMPRINT",EDGE,{"disambiguationData":[TD([[makeQuery(id+"F18.imprint","INTERSECT",VERTEX,{"derivedFrom":[sQuery(id+"F18.wireOp",EDGE,"E58"),subQ0]}),1.0]])],"derivedFrom":subQ0})])],"isStart":true});}
            var Q1;
            {var subQ0=sQuery(id+"F18.wireOp",EDGE,"E61");Q1=makeQuery(id+"F20.opExtrude","CAP_EDGE",EDGE,{"disambiguationData":[OSD([subQ0]),TDD([makeQuery(id+"F18.imprint","IMPRINT",EDGE,{"disambiguationData":[TD([[makeQuery(id+"F18.imprint","INTERSECT",VERTEX,{"derivedFrom":[sQuery(id+"F18.wireOp",EDGE,"E56"),subQ0]}),-1.0]])],"derivedFrom":subQ0})])],"isStart":true});}
            var Q2;
            {var subQ0=sQuery(id+"F18.wireOp",EDGE,"E61");Q2=makeQuery(id+"F20.opExtrude","CAP_EDGE",EDGE,{"disambiguationData":[OSD([subQ0]),TDD([makeQuery(id+"F18.imprint","IMPRINT",EDGE,{"disambiguationData":[TD([[makeQuery(id+"F18.imprint","INTERSECT",VERTEX,{"derivedFrom":[sQuery(id+"F18.wireOp",EDGE,"E54"),subQ0]}),-1.0]])],"derivedFrom":subQ0})])],"isStart":true});}
            var Q3;
            {var subQ0=sQuery(id+"F18.wireOp",EDGE,"E61");Q3=makeQuery(id+"F20.opExtrude","CAP_EDGE",EDGE,{"disambiguationData":[OSD([subQ0]),TDD([makeQuery(id+"F18.imprint","IMPRINT",EDGE,{"disambiguationData":[TD([[makeQuery(id+"F18.imprint","INTERSECT",VERTEX,{"derivedFrom":[sQuery(id+"F18.wireOp",EDGE,"E58"),subQ0]}),1.0]])],"derivedFrom":subQ0})])],"isStart":false});}
            var Q4;
            {var subQ0=sQuery(id+"F18.wireOp",EDGE,"E61");Q4=makeQuery(id+"F20.opExtrude","CAP_EDGE",EDGE,{"disambiguationData":[OSD([subQ0]),TDD([makeQuery(id+"F18.imprint","IMPRINT",EDGE,{"disambiguationData":[TD([[makeQuery(id+"F18.imprint","INTERSECT",VERTEX,{"derivedFrom":[sQuery(id+"F18.wireOp",EDGE,"E56"),subQ0]}),-1.0]])],"derivedFrom":subQ0})])],"isStart":false});}
            var Q5;
            {var subQ0=sQuery(id+"F18.wireOp",EDGE,"E61");Q5=makeQuery(id+"F20.opExtrude","CAP_EDGE",EDGE,{"disambiguationData":[OSD([subQ0]),TDD([makeQuery(id+"F18.imprint","IMPRINT",EDGE,{"disambiguationData":[TD([[makeQuery(id+"F18.imprint","INTERSECT",VERTEX,{"derivedFrom":[sQuery(id+"F18.wireOp",EDGE,"E54"),subQ0]}),-1.0]])],"derivedFrom":subQ0})])],"isStart":false});}
            var Q6;
            Q6=makeQuery(id+"F20.opExtrude","SWEPT_EDGE",EDGE,{"disambiguationData":[OSD([sQuery(id+"F18.wireOp",EDGE,"E42.top"),sQuery(id+"F18.wireOp",EDGE,"E42.right")])]});
            var Q7;
            Q7=makeQuery(id+"F20.opExtrude","SWEPT_EDGE",EDGE,{"disambiguationData":[OSD([sQuery(id+"F18.wireOp",EDGE,"E42.top"),sQuery(id+"F18.wireOp",EDGE,"E42.left")])]});
            var Q8;
            {var subQ0=sQuery(id+"F18.wireOp",EDGE,"E76");Q8=makeQuery(id+"F19.opExtrude","CAP_EDGE",EDGE,{"disambiguationData":[OSD([subQ0]),TDD([makeQuery(id+"F18.imprint","IMPRINT",EDGE,{"disambiguationData":[TD([[makeQuery(id+"F18.imprint","INTERSECT",VERTEX,{"derivedFrom":[sQuery(id+"F18.wireOp",EDGE,"E71"),subQ0]}),-1.0]])],"derivedFrom":subQ0})])],"isStart":true});}
            var Q9;
            {var subQ0=sQuery(id+"F18.wireOp",EDGE,"E76");Q9=makeQuery(id+"F19.opExtrude","CAP_EDGE",EDGE,{"disambiguationData":[OSD([subQ0]),TDD([makeQuery(id+"F18.imprint","IMPRINT",EDGE,{"disambiguationData":[TD([[makeQuery(id+"F18.imprint","INTERSECT",VERTEX,{"derivedFrom":[sQuery(id+"F18.wireOp",EDGE,"E46.right"),subQ0]}),1.0]])],"derivedFrom":subQ0})])],"isStart":true});}
            var Q10;
            {var subQ0=sQuery(id+"F18.wireOp",EDGE,"E76");Q10=makeQuery(id+"F19.opExtrude","CAP_EDGE",EDGE,{"disambiguationData":[OSD([subQ0]),TDD([makeQuery(id+"F18.imprint","IMPRINT",EDGE,{"disambiguationData":[TD([[makeQuery(id+"F18.imprint","INTERSECT",VERTEX,{"derivedFrom":[sQuery(id+"F18.wireOp",EDGE,"E75"),subQ0]}),-1.0]])],"derivedFrom":subQ0})])],"isStart":true});}
            var Q11;
            {var subQ0=sQuery(id+"F18.wireOp",EDGE,"E76");Q11=makeQuery(id+"F19.opExtrude","CAP_EDGE",EDGE,{"disambiguationData":[OSD([subQ0]),TDD([makeQuery(id+"F18.imprint","IMPRINT",EDGE,{"disambiguationData":[TD([[makeQuery(id+"F18.imprint","INTERSECT",VERTEX,{"derivedFrom":[sQuery(id+"F18.wireOp",EDGE,"E69"),subQ0]}),-1.0]])],"derivedFrom":subQ0})])],"isStart":true});}
            var Q12;
            {var subQ0=sQuery(id+"F18.wireOp",EDGE,"E76");Q12=makeQuery(id+"F19.opExtrude","CAP_EDGE",EDGE,{"disambiguationData":[OSD([subQ0]),TDD([makeQuery(id+"F18.imprint","IMPRINT",EDGE,{"disambiguationData":[TD([[makeQuery(id+"F18.imprint","INTERSECT",VERTEX,{"derivedFrom":[sQuery(id+"F18.wireOp",EDGE,"E46.right"),subQ0]}),1.0]])],"derivedFrom":subQ0})])],"isStart":false});}
            var Q13;
            {var subQ0=sQuery(id+"F18.wireOp",EDGE,"E76");Q13=makeQuery(id+"F19.opExtrude","CAP_EDGE",EDGE,{"disambiguationData":[OSD([subQ0]),TDD([makeQuery(id+"F18.imprint","IMPRINT",EDGE,{"disambiguationData":[TD([[makeQuery(id+"F18.imprint","INTERSECT",VERTEX,{"derivedFrom":[sQuery(id+"F18.wireOp",EDGE,"E71"),subQ0]}),-1.0]])],"derivedFrom":subQ0})])],"isStart":false});}
            var Q14;
            {var subQ0=sQuery(id+"F18.wireOp",EDGE,"E76");Q14=makeQuery(id+"F19.opExtrude","CAP_EDGE",EDGE,{"disambiguationData":[OSD([subQ0]),TDD([makeQuery(id+"F18.imprint","IMPRINT",EDGE,{"disambiguationData":[TD([[makeQuery(id+"F18.imprint","INTERSECT",VERTEX,{"derivedFrom":[sQuery(id+"F18.wireOp",EDGE,"E69"),subQ0]}),-1.0]])],"derivedFrom":subQ0})])],"isStart":false});}
            var Q15;
            {var subQ0=sQuery(id+"F18.wireOp",EDGE,"E76");Q15=makeQuery(id+"F19.opExtrude","CAP_EDGE",EDGE,{"disambiguationData":[OSD([subQ0]),TDD([makeQuery(id+"F18.imprint","IMPRINT",EDGE,{"disambiguationData":[TD([[makeQuery(id+"F18.imprint","INTERSECT",VERTEX,{"derivedFrom":[sQuery(id+"F18.wireOp",EDGE,"E75"),subQ0]}),-1.0]])],"derivedFrom":subQ0})])],"isStart":false});}
            var Q16;
            Q16=makeQuery(id+"F19.opExtrude","SWEPT_EDGE",EDGE,{"disambiguationData":[OSD([sQuery(id+"F18.wireOp",EDGE,"E40.top"),sQuery(id+"F18.wireOp",EDGE,"E40.left")])]});
            var Q17;
            Q17=makeQuery(id+"F19.opExtrude","SWEPT_EDGE",EDGE,{"disambiguationData":[OSD([sQuery(id+"F18.wireOp",EDGE,"E40.top"),sQuery(id+"F18.wireOp",EDGE,"E40.right")])]});
            var Q18;
            {var subQ0=sQuery(id+"F18.wireOp",EDGE,"E74");Q18=makeQuery(id+"F20.opExtrude","CAP_EDGE",EDGE,{"disambiguationData":[OSD([subQ0]),TDD([makeQuery(id+"F18.imprint","IMPRINT",EDGE,{"disambiguationData":[TD([[makeQuery(id+"F18.imprint","INTERSECT",VERTEX,{"derivedFrom":[sQuery(id+"F18.wireOp",EDGE,"E68"),subQ0]}),-1.0]])],"derivedFrom":subQ0})])],"isStart":true});}
            var Q19;
            {var subQ0=sQuery(id+"F18.wireOp",EDGE,"E74");Q19=makeQuery(id+"F20.opExtrude","CAP_EDGE",EDGE,{"disambiguationData":[OSD([subQ0]),TDD([makeQuery(id+"F18.imprint","IMPRINT",EDGE,{"disambiguationData":[TD([[makeQuery(id+"F18.imprint","INTERSECT",VERTEX,{"derivedFrom":[sQuery(id+"F18.wireOp",EDGE,"E70"),subQ0]}),-1.0]])],"derivedFrom":subQ0})])],"isStart":true});}
            var Q20;
            {var subQ0=sQuery(id+"F18.wireOp",EDGE,"E74");Q20=makeQuery(id+"F20.opExtrude","CAP_EDGE",EDGE,{"disambiguationData":[OSD([subQ0]),TDD([makeQuery(id+"F18.imprint","IMPRINT",EDGE,{"disambiguationData":[TD([[makeQuery(id+"F18.imprint","INTERSECT",VERTEX,{"derivedFrom":[sQuery(id+"F18.wireOp",EDGE,"E68"),subQ0]}),-1.0]])],"derivedFrom":subQ0})])],"isStart":false});}
            var Q21;
            {var subQ0=sQuery(id+"F18.wireOp",EDGE,"E74");Q21=makeQuery(id+"F20.opExtrude","CAP_EDGE",EDGE,{"disambiguationData":[OSD([subQ0]),TDD([makeQuery(id+"F18.imprint","IMPRINT",EDGE,{"disambiguationData":[TD([[makeQuery(id+"F18.imprint","INTERSECT",VERTEX,{"derivedFrom":[sQuery(id+"F18.wireOp",EDGE,"E70"),subQ0]}),-1.0]])],"derivedFrom":subQ0})])],"isStart":false});}
            var Q22;
            {var subQ0=sQuery(id+"F18.wireOp",EDGE,"E74");Q22=makeQuery(id+"F20.opExtrude","CAP_EDGE",EDGE,{"disambiguationData":[OSD([subQ0]),TDD([makeQuery(id+"F18.imprint","IMPRINT",EDGE,{"disambiguationData":[TD([[makeQuery(id+"F18.imprint","INTERSECT",VERTEX,{"derivedFrom":[sQuery(id+"F18.wireOp",EDGE,"E72"),subQ0]}),-1.0]])],"derivedFrom":subQ0})])],"isStart":true});}
            var Q23;
            {var subQ0=sQuery(id+"F18.wireOp",EDGE,"E74");Q23=makeQuery(id+"F20.opExtrude","CAP_EDGE",EDGE,{"disambiguationData":[OSD([subQ0]),TDD([makeQuery(id+"F18.imprint","IMPRINT",EDGE,{"disambiguationData":[TD([[makeQuery(id+"F18.imprint","INTERSECT",VERTEX,{"derivedFrom":[sQuery(id+"F18.wireOp",EDGE,"E72"),subQ0]}),-1.0]])],"derivedFrom":subQ0})])],"isStart":false});}
            var Q24;
            Q24=makeQuery(id+"F20.opExtrude","SWEPT_EDGE",EDGE,{"disambiguationData":[OSD([sQuery(id+"F18.wireOp",EDGE,"E41.top"),sQuery(id+"F18.wireOp",EDGE,"E41.right")])]});
            var Q25;
            Q25=makeQuery(id+"F20.opExtrude","SWEPT_EDGE",EDGE,{"disambiguationData":[OSD([sQuery(id+"F18.wireOp",EDGE,"E41.top"),sQuery(id+"F18.wireOp",EDGE,"E41.left")])]});
            var Q26;
            {var subQ0=sQuery(id+"F18.wireOp",EDGE,"E60");Q26=makeQuery(id+"F19.opExtrude","CAP_EDGE",EDGE,{"disambiguationData":[OSD([subQ0]),TDD([makeQuery(id+"F18.imprint","IMPRINT",EDGE,{"disambiguationData":[TD([[makeQuery(id+"F18.imprint","INTERSECT",VERTEX,{"derivedFrom":[sQuery(id+"F18.wireOp",EDGE,"E57"),subQ0]}),-1.0]])],"derivedFrom":subQ0})])],"isStart":false});}
            var Q27;
            {var subQ0=sQuery(id+"F18.wireOp",EDGE,"E60");Q27=makeQuery(id+"F19.opExtrude","CAP_EDGE",EDGE,{"disambiguationData":[OSD([subQ0]),TDD([makeQuery(id+"F18.imprint","IMPRINT",EDGE,{"disambiguationData":[TD([[makeQuery(id+"F18.imprint","INTERSECT",VERTEX,{"derivedFrom":[sQuery(id+"F18.wireOp",EDGE,"E57"),subQ0]}),-1.0]])],"derivedFrom":subQ0})])],"isStart":true});}
            var Q28;
            {var subQ0=sQuery(id+"F18.wireOp",EDGE,"E60");Q28=makeQuery(id+"F19.opExtrude","CAP_EDGE",EDGE,{"disambiguationData":[OSD([subQ0]),TDD([makeQuery(id+"F18.imprint","IMPRINT",EDGE,{"disambiguationData":[TD([[makeQuery(id+"F18.imprint","INTERSECT",VERTEX,{"derivedFrom":[sQuery(id+"F18.wireOp",EDGE,"E55"),subQ0]}),-1.0]])],"derivedFrom":subQ0})])],"isStart":false});}
            var Q29;
            {var subQ0=sQuery(id+"F18.wireOp",EDGE,"E60");Q29=makeQuery(id+"F19.opExtrude","CAP_EDGE",EDGE,{"disambiguationData":[OSD([subQ0]),TDD([makeQuery(id+"F18.imprint","IMPRINT",EDGE,{"disambiguationData":[TD([[makeQuery(id+"F18.imprint","INTERSECT",VERTEX,{"derivedFrom":[sQuery(id+"F18.wireOp",EDGE,"E55"),subQ0]}),-1.0]])],"derivedFrom":subQ0})])],"isStart":true});}
            var Q30;
            {var subQ0=sQuery(id+"F18.wireOp",EDGE,"E60");Q30=makeQuery(id+"F19.opExtrude","CAP_EDGE",EDGE,{"disambiguationData":[OSD([subQ0]),TDD([makeQuery(id+"F18.imprint","IMPRINT",EDGE,{"disambiguationData":[TD([[makeQuery(id+"F18.imprint","INTERSECT",VERTEX,{"derivedFrom":[sQuery(id+"F18.wireOp",EDGE,"E44.left"),subQ0]}),-1.0]])],"derivedFrom":subQ0})])],"isStart":false});}
            var Q31;
            {var subQ0=sQuery(id+"F18.wireOp",EDGE,"E60");Q31=makeQuery(id+"F19.opExtrude","CAP_EDGE",EDGE,{"disambiguationData":[OSD([subQ0]),TDD([makeQuery(id+"F18.imprint","IMPRINT",EDGE,{"disambiguationData":[TD([[makeQuery(id+"F18.imprint","INTERSECT",VERTEX,{"derivedFrom":[sQuery(id+"F18.wireOp",EDGE,"E44.left"),subQ0]}),-1.0]])],"derivedFrom":subQ0})])],"isStart":true});}
            var Q32;
            {var subQ0=sQuery(id+"F18.wireOp",EDGE,"E60");Q32=makeQuery(id+"F19.opExtrude","CAP_EDGE",EDGE,{"disambiguationData":[OSD([subQ0]),TDD([makeQuery(id+"F18.imprint","IMPRINT",EDGE,{"disambiguationData":[TD([[makeQuery(id+"F18.imprint","INTERSECT",VERTEX,{"derivedFrom":[sQuery(id+"F18.wireOp",EDGE,"E44.right"),subQ0]}),1.0]])],"derivedFrom":subQ0})])],"isStart":true});}
            var Q33;
            {var subQ0=sQuery(id+"F18.wireOp",EDGE,"E60");Q33=makeQuery(id+"F19.opExtrude","CAP_EDGE",EDGE,{"disambiguationData":[OSD([subQ0]),TDD([makeQuery(id+"F18.imprint","IMPRINT",EDGE,{"disambiguationData":[TD([[makeQuery(id+"F18.imprint","INTERSECT",VERTEX,{"derivedFrom":[sQuery(id+"F18.wireOp",EDGE,"E44.right"),subQ0]}),1.0]])],"derivedFrom":subQ0})])],"isStart":false});}
            var Q34;
            Q34=makeQuery(id+"F19.opExtrude","SWEPT_EDGE",EDGE,{"disambiguationData":[OSD([sQuery(id+"F18.wireOp",EDGE,"E39.top"),sQuery(id+"F18.wireOp",EDGE,"E39.right")])]});
            var Q35;
            Q35=makeQuery(id+"F19.opExtrude","SWEPT_EDGE",EDGE,{"disambiguationData":[OSD([sQuery(id+"F18.wireOp",EDGE,"E39.top"),sQuery(id+"F18.wireOp",EDGE,"E39.left")])]});
            fillet(context, id + "F21", {"entities" : qUnion([Q0, Q1, Q2, Q3, Q4, Q5, Q6, Q7, Q8, Q9, Q10, Q11, Q12, Q13, Q14, Q15, Q16, Q17, Q18, Q19, Q20, Q21, Q22, Q23, Q24, Q25, Q26, Q27, Q28, Q29, Q30, Q31, Q32, Q33, Q34, Q35]), "radius" : 3.17 * mm, "tangentPropagation" : true, "allowEdgeOverflow" : false});
        }
        {
            var Q0;
            Q0=makeQuery(id+"F19.opExtrude","SWEPT_FACE",FACE,{"disambiguationData":[OSD([sQuery(id+"F18.wireOp",EDGE,"E39.left"),sQuery(id+"F18.wireOp",EDGE,"E44.left")])]});
            var sketch = newSketch(context, id + "F22", { "sketchPlane" : qUnion([Q0])});
            skCircle(sketch, "E77", {"center": v(111.13, 85.66) * mm, "radius": 1.59 * mm});
            skSolve(sketch);
        }
        {
            var Q0;
            Q0=makeQuery(id+"F22.imprint","IMPRINT",FACE,{"disambiguationData":[TD([[makeQuery(id+"F22.imprint","IMPRINT",EDGE,{"derivedFrom":sQuery(id+"F22.wireOp",EDGE,"E77")}),1.0]])]});
            extrude(context, id + "F23", {"entities" : qUnion([Q0]), "operationType" : NewBodyOperationType.REMOVE, "endBound" : BoundingType.THROUGH_ALL, "oppositeDirection" : true, "depth" : 25.4 * mm});
        }
        {
            var Q0;
            Q0=makeQuery(id+"F19.opExtrude","SWEPT_FACE",FACE,{"disambiguationData":[OSD([sQuery(id+"F18.wireOp",EDGE,"E40.left"),sQuery(id+"F18.wireOp",EDGE,"E46.right")])]});
            var sketch = newSketch(context, id + "F24", { "sketchPlane" : qUnion([Q0])});
            skCircle(sketch, "E78", {"center": v(-111.13, 85.73) * mm, "radius": 1.59 * mm});
            skSolve(sketch);
        }
        {
            var Q0;
            Q0=makeQuery(id+"F24.imprint","IMPRINT",FACE,{"disambiguationData":[TD([[makeQuery(id+"F24.imprint","IMPRINT",EDGE,{"derivedFrom":sQuery(id+"F24.wireOp",EDGE,"E78")}),1.0]])]});
            extrude(context, id + "F25", {"entities" : qUnion([Q0]), "operationType" : NewBodyOperationType.REMOVE, "endBound" : BoundingType.THROUGH_ALL, "oppositeDirection" : true, "depth" : 25.4 * mm});
        }
        {
            var Q0;
            Q0=makeQuery(id+"F24.imprint","IMPRINT",FACE,{"disambiguationData":[TD([[makeQuery(id+"F24.imprint","IMPRINT",EDGE,{"derivedFrom":sQuery(id+"F24.wireOp",EDGE,"E78")}),1.0]])]});
            var Q1;
            Q1=makeQuery(id+"F19.opExtrude","SWEPT_FACE",FACE,{"disambiguationData":[OSD([sQuery(id+"F18.wireOp",EDGE,"E40.right"),sQuery(id+"F18.wireOp",EDGE,"E46.left"),sQuery(id+"F18.wireOp",EDGE,"E75")])]});
            extrude(context, id + "F26", {"entities" : qUnion([Q0]), "endBound" : BoundingType.UP_TO_SURFACE, "oppositeDirection" : true, "endBoundEntityFace" : qUnion([Q1]), "depth" : 25.4 * mm});
        }
        {
            var Q0;
            Q0=makeQuery(id+"F22.imprint","IMPRINT",FACE,{"disambiguationData":[TD([[makeQuery(id+"F22.imprint","IMPRINT",EDGE,{"derivedFrom":sQuery(id+"F22.wireOp",EDGE,"E77")}),1.0]])]});
            var Q1;
            Q1=makeQuery(id+"F19.opExtrude","SWEPT_FACE",FACE,{"disambiguationData":[OSD([sQuery(id+"F18.wireOp",EDGE,"E39.right"),sQuery(id+"F18.wireOp",EDGE,"E44.right")])]});
            extrude(context, id + "F27", {"entities" : qUnion([Q0]), "endBound" : BoundingType.UP_TO_SURFACE, "oppositeDirection" : true, "endBoundEntityFace" : qUnion([Q1]), "depth" : 25.4 * mm});
        }
        {
            var Q0;
            Q0=makeQuery(id+"F18.imprint","IMPRINT",FACE,{"disambiguationData":[TD([[makeQuery(id+"F18.imprint","IMPRINT",EDGE,{"derivedFrom":sQuery(id+"F18.wireOp",EDGE,"E39.top")}),1.0]])]});
            var Q1;
            {var subQ4=sQuery(id+"F18.wireOp",EDGE,"E42.top");Q1=makeQuery(id+"F18.imprint","IMPRINT",FACE,{"disambiguationData":[TD([[makeQuery(id+"F18.imprint","IMPRINT",EDGE,{"derivedFrom":subQ4}),1.0]])]});}
            var Q2;
            {var subQ0=sQuery(id+"F18.wireOp",EDGE,"E44.bottom");Q2=makeQuery(id+"F18.imprint","IMPRINT",FACE,{"disambiguationData":[TD([[makeQuery(id+"F18.imprint","IMPRINT",EDGE,{"derivedFrom":subQ0}),1.0]])]});}
            var Q3;
            {var subQ1=sQuery(id+"F18.wireOp",EDGE,"E42.bottom");var subQ3=sQuery(id+"F18.wireOp",EDGE,"E54");var subQ4=makeQuery(id+"F18.imprint","INTERSECT",VERTEX,{"derivedFrom":[subQ1,subQ3]});Q3=makeQuery(id+"F18.imprint","IMPRINT",FACE,{"disambiguationData":[TD([[makeQuery(id+"F18.imprint","IMPRINT",EDGE,{"disambiguationData":[TD([[subQ4,1.0]])],"derivedFrom":subQ3}),1.0]])]});}
            var Q4;
            {var subQ1=sQuery(id+"F18.wireOp",EDGE,"E42.bottom");var subQ3=sQuery(id+"F18.wireOp",EDGE,"E54");var subQ4=makeQuery(id+"F18.imprint","INTERSECT",VERTEX,{"derivedFrom":[subQ1,subQ3]});Q4=makeQuery(id+"F18.imprint","IMPRINT",FACE,{"disambiguationData":[TD([[makeQuery(id+"F18.imprint","IMPRINT",EDGE,{"disambiguationData":[TD([[subQ4,-1.0]])],"derivedFrom":subQ3}),1.0]])]});}
            var Q5;
            {var subQ1=sQuery(id+"F18.wireOp",EDGE,"E44.top");var subQ3=sQuery(id+"F18.wireOp",EDGE,"E54");var subQ4=makeQuery(id+"F18.imprint","INTERSECT",VERTEX,{"derivedFrom":[subQ1,subQ3]});Q5=makeQuery(id+"F18.imprint","IMPRINT",FACE,{"disambiguationData":[TD([[makeQuery(id+"F18.imprint","IMPRINT",EDGE,{"disambiguationData":[TD([[subQ4,1.0]])],"derivedFrom":subQ3}),1.0]])]});}
            var Q6;
            {var subQ0=sQuery(id+"F18.wireOp",EDGE,"E54");var subQ1=sQuery(id+"F18.wireOp",EDGE,"E44.top");var subQ2=makeQuery(id+"F18.imprint","INTERSECT",VERTEX,{"derivedFrom":[subQ1,subQ0]});Q6=makeQuery(id+"F18.imprint","IMPRINT",FACE,{"disambiguationData":[TD([[makeQuery(id+"F18.imprint","IMPRINT",EDGE,{"disambiguationData":[TD([[subQ2,-1.0]])],"derivedFrom":subQ1}),-1.0]])]});}
            var Q7;
            {var subQ0=sQuery(id+"F18.wireOp",EDGE,"E54");var subQ1=sQuery(id+"F18.wireOp",EDGE,"E42.bottom");var subQ2=makeQuery(id+"F18.imprint","INTERSECT",VERTEX,{"derivedFrom":[subQ1,subQ0]});Q7=makeQuery(id+"F18.imprint","IMPRINT",FACE,{"disambiguationData":[TD([[makeQuery(id+"F18.imprint","IMPRINT",EDGE,{"disambiguationData":[TD([[subQ2,-1.0]])],"derivedFrom":subQ1}),1.0]])]});}
            var Q8;
            {var subQ0=sQuery(id+"F18.wireOp",EDGE,"E54");var subQ1=sQuery(id+"F18.wireOp",EDGE,"E42.bottom");var subQ2=makeQuery(id+"F18.imprint","INTERSECT",VERTEX,{"derivedFrom":[subQ1,subQ0]});Q8=makeQuery(id+"F18.imprint","IMPRINT",FACE,{"disambiguationData":[TD([[makeQuery(id+"F18.imprint","IMPRINT",EDGE,{"disambiguationData":[TD([[subQ2,-1.0]])],"derivedFrom":subQ1}),-1.0]])]});}
            var Q9;
            {var subQ0=sQuery(id+"F18.wireOp",EDGE,"E53");Q9=makeQuery(id+"F18.imprint","IMPRINT",FACE,{"disambiguationData":[TD([[makeQuery(id+"F18.imprint","IMPRINT",EDGE,{"derivedFrom":subQ0}),-1.0]])]});}
            var Q10;
            {var subQ0=sQuery(id+"F18.wireOp",EDGE,"E47");Q10=makeQuery(id+"F18.imprint","IMPRINT",FACE,{"disambiguationData":[TD([[makeQuery(id+"F18.imprint","IMPRINT",EDGE,{"derivedFrom":subQ0}),-1.0]])]});}
            var Q11;
            {var subQ1=sQuery(id+"F18.wireOp",EDGE,"E42.bottom");var subQ3=sQuery(id+"F18.wireOp",EDGE,"E58");var subQ4=makeQuery(id+"F18.imprint","INTERSECT",VERTEX,{"derivedFrom":[subQ1,subQ3]});Q11=makeQuery(id+"F18.imprint","IMPRINT",FACE,{"disambiguationData":[TD([[makeQuery(id+"F18.imprint","IMPRINT",EDGE,{"disambiguationData":[TD([[subQ4,1.0]])],"derivedFrom":subQ3}),-1.0]])]});}
            var Q12;
            {var subQ1=sQuery(id+"F18.wireOp",EDGE,"E42.bottom");var subQ3=sQuery(id+"F18.wireOp",EDGE,"E58");var subQ4=makeQuery(id+"F18.imprint","INTERSECT",VERTEX,{"derivedFrom":[subQ1,subQ3]});Q12=makeQuery(id+"F18.imprint","IMPRINT",FACE,{"disambiguationData":[TD([[makeQuery(id+"F18.imprint","IMPRINT",EDGE,{"disambiguationData":[TD([[subQ4,-1.0]])],"derivedFrom":subQ3}),-1.0]])]});}
            var Q13;
            {var subQ1=sQuery(id+"F18.wireOp",EDGE,"E44.top");var subQ3=sQuery(id+"F18.wireOp",EDGE,"E58");var subQ4=makeQuery(id+"F18.imprint","INTERSECT",VERTEX,{"derivedFrom":[subQ1,subQ3]});Q13=makeQuery(id+"F18.imprint","IMPRINT",FACE,{"disambiguationData":[TD([[makeQuery(id+"F18.imprint","IMPRINT",EDGE,{"disambiguationData":[TD([[subQ4,1.0]])],"derivedFrom":subQ3}),-1.0]])]});}
            var Q14;
            {var subQ0=sQuery(id+"F18.wireOp",EDGE,"E59");var subQ1=sQuery(id+"F18.wireOp",EDGE,"E42.bottom");var subQ2=makeQuery(id+"F18.imprint","INTERSECT",VERTEX,{"derivedFrom":[subQ1,subQ0]});Q14=makeQuery(id+"F18.imprint","IMPRINT",FACE,{"disambiguationData":[TD([[makeQuery(id+"F18.imprint","IMPRINT",EDGE,{"disambiguationData":[TD([[subQ2,-1.0]])],"derivedFrom":subQ1}),1.0]])]});}
            var Q15;
            {var subQ0=sQuery(id+"F18.wireOp",EDGE,"E58");var subQ1=sQuery(id+"F18.wireOp",EDGE,"E44.top");var subQ2=makeQuery(id+"F18.imprint","INTERSECT",VERTEX,{"derivedFrom":[subQ1,subQ0]});Q15=makeQuery(id+"F18.imprint","IMPRINT",FACE,{"disambiguationData":[TD([[makeQuery(id+"F18.imprint","IMPRINT",EDGE,{"disambiguationData":[TD([[subQ2,1.0]])],"derivedFrom":subQ1}),-1.0]])]});}
            var Q16;
            {var subQ0=sQuery(id+"F18.wireOp",EDGE,"E48");Q16=makeQuery(id+"F18.imprint","IMPRINT",FACE,{"disambiguationData":[TD([[makeQuery(id+"F18.imprint","IMPRINT",EDGE,{"derivedFrom":subQ0}),-1.0]])]});}
            var Q17;
            {var subQ0=sQuery(id+"F18.wireOp",EDGE,"E59");var subQ1=sQuery(id+"F18.wireOp",EDGE,"E42.bottom");var subQ2=makeQuery(id+"F18.imprint","INTERSECT",VERTEX,{"derivedFrom":[subQ1,subQ0]});Q17=makeQuery(id+"F18.imprint","IMPRINT",FACE,{"disambiguationData":[TD([[makeQuery(id+"F18.imprint","IMPRINT",EDGE,{"disambiguationData":[TD([[subQ2,-1.0]])],"derivedFrom":subQ1}),-1.0]])]});}
            var Q18;
            {var subQ0=sQuery(id+"F18.wireOp",EDGE,"E57");var subQ1=sQuery(id+"F18.wireOp",EDGE,"E44.top");var subQ2=makeQuery(id+"F18.imprint","INTERSECT",VERTEX,{"derivedFrom":[subQ1,subQ0]});Q18=makeQuery(id+"F18.imprint","IMPRINT",FACE,{"disambiguationData":[TD([[makeQuery(id+"F18.imprint","IMPRINT",EDGE,{"disambiguationData":[TD([[subQ2,-1.0]])],"derivedFrom":subQ1}),-1.0]])]});}
            var Q19;
            {var subQ0=sQuery(id+"F18.wireOp",EDGE,"E57");var subQ1=sQuery(id+"F18.wireOp",EDGE,"E42.bottom");var subQ2=makeQuery(id+"F18.imprint","INTERSECT",VERTEX,{"derivedFrom":[subQ1,subQ0]});Q19=makeQuery(id+"F18.imprint","IMPRINT",FACE,{"disambiguationData":[TD([[makeQuery(id+"F18.imprint","IMPRINT",EDGE,{"disambiguationData":[TD([[subQ2,-1.0]])],"derivedFrom":subQ1}),1.0]])]});}
            var Q20;
            {var subQ0=sQuery(id+"F18.wireOp",EDGE,"E57");var subQ1=sQuery(id+"F18.wireOp",EDGE,"E42.bottom");var subQ2=makeQuery(id+"F18.imprint","INTERSECT",VERTEX,{"derivedFrom":[subQ1,subQ0]});Q20=makeQuery(id+"F18.imprint","IMPRINT",FACE,{"disambiguationData":[TD([[makeQuery(id+"F18.imprint","IMPRINT",EDGE,{"disambiguationData":[TD([[subQ2,-1.0]])],"derivedFrom":subQ1}),-1.0]])]});}
            var Q21;
            {var subQ1=sQuery(id+"F18.wireOp",EDGE,"E51");var subQ5=makeQuery(id+"F18.imprint","IMPRINT",VERTEX,{"derivedFrom":subQ1});Q21=makeQuery(id+"F18.imprint","IMPRINT",FACE,{"disambiguationData":[TD([[makeQuery(id+"F18.imprint","IMPRINT",EDGE,{"disambiguationData":[TD([[subQ5,1.0]])],"derivedFrom":subQ1}),-1.0]])]});}
            var Q22;
            {var subQ0=sQuery(id+"F18.wireOp",EDGE,"E56");var subQ1=sQuery(id+"F18.wireOp",EDGE,"E42.bottom");var subQ2=makeQuery(id+"F18.imprint","INTERSECT",VERTEX,{"derivedFrom":[subQ1,subQ0]});Q22=makeQuery(id+"F18.imprint","IMPRINT",FACE,{"disambiguationData":[TD([[makeQuery(id+"F18.imprint","IMPRINT",EDGE,{"disambiguationData":[TD([[subQ2,-1.0]])],"derivedFrom":subQ1}),-1.0]])]});}
            var Q23;
            {var subQ0=sQuery(id+"F18.wireOp",EDGE,"E56");var subQ1=sQuery(id+"F18.wireOp",EDGE,"E42.bottom");var subQ2=makeQuery(id+"F18.imprint","INTERSECT",VERTEX,{"derivedFrom":[subQ1,subQ0]});Q23=makeQuery(id+"F18.imprint","IMPRINT",FACE,{"disambiguationData":[TD([[makeQuery(id+"F18.imprint","IMPRINT",EDGE,{"disambiguationData":[TD([[subQ2,-1.0]])],"derivedFrom":subQ1}),1.0]])]});}
            var Q24;
            {var subQ0=sQuery(id+"F18.wireOp",EDGE,"E56");var subQ1=sQuery(id+"F18.wireOp",EDGE,"E44.top");var subQ2=makeQuery(id+"F18.imprint","INTERSECT",VERTEX,{"derivedFrom":[subQ1,subQ0]});Q24=makeQuery(id+"F18.imprint","IMPRINT",FACE,{"disambiguationData":[TD([[makeQuery(id+"F18.imprint","IMPRINT",EDGE,{"disambiguationData":[TD([[subQ2,-1.0]])],"derivedFrom":subQ1}),-1.0]])]});}
            var Q25;
            {var subQ0=sQuery(id+"F18.wireOp",EDGE,"E55");var subQ1=sQuery(id+"F18.wireOp",EDGE,"E44.top");var subQ2=makeQuery(id+"F18.imprint","INTERSECT",VERTEX,{"derivedFrom":[subQ1,subQ0]});Q25=makeQuery(id+"F18.imprint","IMPRINT",FACE,{"disambiguationData":[TD([[makeQuery(id+"F18.imprint","IMPRINT",EDGE,{"disambiguationData":[TD([[subQ2,-1.0]])],"derivedFrom":subQ1}),-1.0]])]});}
            var Q26;
            {var subQ0=sQuery(id+"F18.wireOp",EDGE,"E55");var subQ1=sQuery(id+"F18.wireOp",EDGE,"E42.bottom");var subQ2=makeQuery(id+"F18.imprint","INTERSECT",VERTEX,{"derivedFrom":[subQ1,subQ0]});Q26=makeQuery(id+"F18.imprint","IMPRINT",FACE,{"disambiguationData":[TD([[makeQuery(id+"F18.imprint","IMPRINT",EDGE,{"disambiguationData":[TD([[subQ2,-1.0]])],"derivedFrom":subQ1}),1.0]])]});}
            var Q27;
            {var subQ0=sQuery(id+"F18.wireOp",EDGE,"E55");var subQ1=sQuery(id+"F18.wireOp",EDGE,"E42.bottom");var subQ2=makeQuery(id+"F18.imprint","INTERSECT",VERTEX,{"derivedFrom":[subQ1,subQ0]});Q27=makeQuery(id+"F18.imprint","IMPRINT",FACE,{"disambiguationData":[TD([[makeQuery(id+"F18.imprint","IMPRINT",EDGE,{"disambiguationData":[TD([[subQ2,-1.0]])],"derivedFrom":subQ1}),-1.0]])]});}
            var Q28;
            {var subQ0=sQuery(id+"F18.wireOp",EDGE,"E52");Q28=makeQuery(id+"F18.imprint","IMPRINT",FACE,{"disambiguationData":[TD([[makeQuery(id+"F18.imprint","IMPRINT",EDGE,{"derivedFrom":subQ0}),-1.0]])]});}
            var Q29;
            {var subQ0=sQuery(id+"F18.wireOp",EDGE,"E50");Q29=makeQuery(id+"F18.imprint","IMPRINT",FACE,{"disambiguationData":[TD([[makeQuery(id+"F18.imprint","IMPRINT",EDGE,{"derivedFrom":subQ0}),-1.0]])]});}
            var Q30;
            {var subQ1=sQuery(id+"F18.wireOp",EDGE,"E46.bottom");var subQ3=sQuery(id+"F18.wireOp",EDGE,"E68");var subQ4=makeQuery(id+"F18.imprint","INTERSECT",VERTEX,{"derivedFrom":[subQ1,subQ3]});Q30=makeQuery(id+"F18.imprint","IMPRINT",FACE,{"disambiguationData":[TD([[makeQuery(id+"F18.imprint","IMPRINT",EDGE,{"disambiguationData":[TD([[subQ4,-1.0]])],"derivedFrom":subQ3}),1.0]])]});}
            var Q31;
            {var subQ0=sQuery(id+"F18.wireOp",EDGE,"E62");Q31=makeQuery(id+"F18.imprint","IMPRINT",FACE,{"disambiguationData":[TD([[makeQuery(id+"F18.imprint","IMPRINT",EDGE,{"derivedFrom":subQ0}),-1.0]])]});}
            var Q32;
            {var subQ0=sQuery(id+"F18.wireOp",EDGE,"E62");Q32=makeQuery(id+"F18.imprint","IMPRINT",FACE,{"disambiguationData":[TD([[makeQuery(id+"F18.imprint","IMPRINT",EDGE,{"derivedFrom":subQ0}),1.0]])]});}
            var Q33;
            {var subQ1=sQuery(id+"F18.wireOp",EDGE,"E46.top");var subQ3=sQuery(id+"F18.wireOp",EDGE,"E68");var subQ4=makeQuery(id+"F18.imprint","INTERSECT",VERTEX,{"derivedFrom":[subQ1,subQ3]});Q33=makeQuery(id+"F18.imprint","IMPRINT",FACE,{"disambiguationData":[TD([[makeQuery(id+"F18.imprint","IMPRINT",EDGE,{"disambiguationData":[TD([[subQ4,1.0]])],"derivedFrom":subQ3}),1.0]])]});}
            var Q34;
            {var subQ0=sQuery(id+"F18.wireOp",EDGE,"E68");var subQ1=sQuery(id+"F18.wireOp",EDGE,"E46.top");var subQ2=makeQuery(id+"F18.imprint","INTERSECT",VERTEX,{"derivedFrom":[subQ1,subQ0]});Q34=makeQuery(id+"F18.imprint","IMPRINT",FACE,{"disambiguationData":[TD([[makeQuery(id+"F18.imprint","IMPRINT",EDGE,{"disambiguationData":[TD([[subQ2,-1.0]])],"derivedFrom":subQ1}),-1.0]])]});}
            var Q35;
            {var subQ0=sQuery(id+"F18.wireOp",EDGE,"E63");Q35=makeQuery(id+"F18.imprint","IMPRINT",FACE,{"disambiguationData":[TD([[makeQuery(id+"F18.imprint","IMPRINT",EDGE,{"derivedFrom":subQ0}),1.0]])]});}
            var Q36;
            {var subQ0=sQuery(id+"F18.wireOp",EDGE,"E63");Q36=makeQuery(id+"F18.imprint","IMPRINT",FACE,{"disambiguationData":[TD([[makeQuery(id+"F18.imprint","IMPRINT",EDGE,{"derivedFrom":subQ0}),-1.0]])]});}
            var Q37;
            {var subQ0=sQuery(id+"F18.wireOp",EDGE,"E68");var subQ1=sQuery(id+"F18.wireOp",EDGE,"E46.bottom");var subQ2=makeQuery(id+"F18.imprint","INTERSECT",VERTEX,{"derivedFrom":[subQ1,subQ0]});Q37=makeQuery(id+"F18.imprint","IMPRINT",FACE,{"disambiguationData":[TD([[makeQuery(id+"F18.imprint","IMPRINT",EDGE,{"disambiguationData":[TD([[subQ2,-1.0]])],"derivedFrom":subQ1}),1.0]])]});}
            var Q38;
            {var subQ0=sQuery(id+"F18.wireOp",EDGE,"E69");var subQ1=sQuery(id+"F18.wireOp",EDGE,"E46.bottom");var subQ2=makeQuery(id+"F18.imprint","INTERSECT",VERTEX,{"derivedFrom":[subQ1,subQ0]});Q38=makeQuery(id+"F18.imprint","IMPRINT",FACE,{"disambiguationData":[TD([[makeQuery(id+"F18.imprint","IMPRINT",EDGE,{"disambiguationData":[TD([[subQ2,-1.0]])],"derivedFrom":subQ1}),1.0]])]});}
            var Q39;
            {var subQ0=sQuery(id+"F18.wireOp",EDGE,"E64");Q39=makeQuery(id+"F18.imprint","IMPRINT",FACE,{"disambiguationData":[TD([[makeQuery(id+"F18.imprint","IMPRINT",EDGE,{"derivedFrom":subQ0}),-1.0]])]});}
            var Q40;
            {var subQ0=sQuery(id+"F18.wireOp",EDGE,"E64");Q40=makeQuery(id+"F18.imprint","IMPRINT",FACE,{"disambiguationData":[TD([[makeQuery(id+"F18.imprint","IMPRINT",EDGE,{"derivedFrom":subQ0}),1.0]])]});}
            var Q41;
            {var subQ0=sQuery(id+"F18.wireOp",EDGE,"E69");var subQ1=sQuery(id+"F18.wireOp",EDGE,"E46.top");var subQ2=makeQuery(id+"F18.imprint","INTERSECT",VERTEX,{"derivedFrom":[subQ1,subQ0]});Q41=makeQuery(id+"F18.imprint","IMPRINT",FACE,{"disambiguationData":[TD([[makeQuery(id+"F18.imprint","IMPRINT",EDGE,{"disambiguationData":[TD([[subQ2,-1.0]])],"derivedFrom":subQ1}),-1.0]])]});}
            var Q42;
            {var subQ0=sQuery(id+"F18.wireOp",EDGE,"E70");var subQ1=sQuery(id+"F18.wireOp",EDGE,"E46.top");var subQ2=makeQuery(id+"F18.imprint","INTERSECT",VERTEX,{"derivedFrom":[subQ1,subQ0]});Q42=makeQuery(id+"F18.imprint","IMPRINT",FACE,{"disambiguationData":[TD([[makeQuery(id+"F18.imprint","IMPRINT",EDGE,{"disambiguationData":[TD([[subQ2,-1.0]])],"derivedFrom":subQ1}),-1.0]])]});}
            var Q43;
            {var subQ0=sQuery(id+"F18.wireOp",EDGE,"E65");Q43=makeQuery(id+"F18.imprint","IMPRINT",FACE,{"disambiguationData":[TD([[makeQuery(id+"F18.imprint","IMPRINT",EDGE,{"derivedFrom":subQ0}),1.0]])]});}
            var Q44;
            {var subQ0=sQuery(id+"F18.wireOp",EDGE,"E65");Q44=makeQuery(id+"F18.imprint","IMPRINT",FACE,{"disambiguationData":[TD([[makeQuery(id+"F18.imprint","IMPRINT",EDGE,{"derivedFrom":subQ0}),-1.0]])]});}
            var Q45;
            {var subQ0=sQuery(id+"F18.wireOp",EDGE,"E70");var subQ1=sQuery(id+"F18.wireOp",EDGE,"E46.bottom");var subQ2=makeQuery(id+"F18.imprint","INTERSECT",VERTEX,{"derivedFrom":[subQ1,subQ0]});Q45=makeQuery(id+"F18.imprint","IMPRINT",FACE,{"disambiguationData":[TD([[makeQuery(id+"F18.imprint","IMPRINT",EDGE,{"disambiguationData":[TD([[subQ2,-1.0]])],"derivedFrom":subQ1}),1.0]])]});}
            var Q46;
            {var subQ0=sQuery(id+"F18.wireOp",EDGE,"E71");var subQ1=sQuery(id+"F18.wireOp",EDGE,"E46.bottom");var subQ2=makeQuery(id+"F18.imprint","INTERSECT",VERTEX,{"derivedFrom":[subQ1,subQ0]});Q46=makeQuery(id+"F18.imprint","IMPRINT",FACE,{"disambiguationData":[TD([[makeQuery(id+"F18.imprint","IMPRINT",EDGE,{"disambiguationData":[TD([[subQ2,-1.0]])],"derivedFrom":subQ1}),1.0]])]});}
            var Q47;
            {var subQ0=sQuery(id+"F18.wireOp",EDGE,"E66");Q47=makeQuery(id+"F18.imprint","IMPRINT",FACE,{"disambiguationData":[TD([[makeQuery(id+"F18.imprint","IMPRINT",EDGE,{"derivedFrom":subQ0}),-1.0]])]});}
            var Q48;
            {var subQ0=sQuery(id+"F18.wireOp",EDGE,"E66");Q48=makeQuery(id+"F18.imprint","IMPRINT",FACE,{"disambiguationData":[TD([[makeQuery(id+"F18.imprint","IMPRINT",EDGE,{"derivedFrom":subQ0}),1.0]])]});}
            var Q49;
            {var subQ0=sQuery(id+"F18.wireOp",EDGE,"E71");var subQ1=sQuery(id+"F18.wireOp",EDGE,"E46.top");var subQ2=makeQuery(id+"F18.imprint","INTERSECT",VERTEX,{"derivedFrom":[subQ1,subQ0]});Q49=makeQuery(id+"F18.imprint","IMPRINT",FACE,{"disambiguationData":[TD([[makeQuery(id+"F18.imprint","IMPRINT",EDGE,{"disambiguationData":[TD([[subQ2,-1.0]])],"derivedFrom":subQ1}),-1.0]])]});}
            var Q50;
            {var subQ0=sQuery(id+"F18.wireOp",EDGE,"E72");var subQ1=sQuery(id+"F18.wireOp",EDGE,"E46.bottom");var subQ2=makeQuery(id+"F18.imprint","INTERSECT",VERTEX,{"derivedFrom":[subQ1,subQ0]});Q50=makeQuery(id+"F18.imprint","IMPRINT",FACE,{"disambiguationData":[TD([[makeQuery(id+"F18.imprint","IMPRINT",EDGE,{"disambiguationData":[TD([[subQ2,-1.0]])],"derivedFrom":subQ1}),1.0]])]});}
            var Q51;
            {var subQ1=sQuery(id+"F18.wireOp",EDGE,"E46.bottom");var subQ3=sQuery(id+"F18.wireOp",EDGE,"E73");var subQ4=makeQuery(id+"F18.imprint","INTERSECT",VERTEX,{"derivedFrom":[subQ1,subQ3]});Q51=makeQuery(id+"F18.imprint","IMPRINT",FACE,{"disambiguationData":[TD([[makeQuery(id+"F18.imprint","IMPRINT",EDGE,{"disambiguationData":[TD([[subQ4,-1.0]])],"derivedFrom":subQ3}),-1.0]])]});}
            var Q52;
            {var subQ0=sQuery(id+"F18.wireOp",EDGE,"E67");Q52=makeQuery(id+"F18.imprint","IMPRINT",FACE,{"disambiguationData":[TD([[makeQuery(id+"F18.imprint","IMPRINT",EDGE,{"derivedFrom":subQ0}),-1.0]])]});}
            var Q53;
            {var subQ0=sQuery(id+"F18.wireOp",EDGE,"E40.bottom");Q53=makeQuery(id+"F18.imprint","IMPRINT",FACE,{"disambiguationData":[TD([[makeQuery(id+"F18.imprint","IMPRINT",EDGE,{"derivedFrom":subQ0}),-1.0]])]});}
            var Q54;
            {var subQ0=sQuery(id+"F18.wireOp",EDGE,"E72");var subQ1=sQuery(id+"F18.wireOp",EDGE,"E46.top");var subQ2=makeQuery(id+"F18.imprint","INTERSECT",VERTEX,{"derivedFrom":[subQ1,subQ0]});Q54=makeQuery(id+"F18.imprint","IMPRINT",FACE,{"disambiguationData":[TD([[makeQuery(id+"F18.imprint","IMPRINT",EDGE,{"disambiguationData":[TD([[subQ2,-1.0]])],"derivedFrom":subQ1}),-1.0]])]});}
            var Q55;
            {var subQ1=sQuery(id+"F18.wireOp",EDGE,"E46.top");var subQ3=sQuery(id+"F18.wireOp",EDGE,"E73");var subQ4=makeQuery(id+"F18.imprint","INTERSECT",VERTEX,{"derivedFrom":[subQ1,subQ3]});Q55=makeQuery(id+"F18.imprint","IMPRINT",FACE,{"disambiguationData":[TD([[makeQuery(id+"F18.imprint","IMPRINT",EDGE,{"disambiguationData":[TD([[subQ4,1.0]])],"derivedFrom":subQ3}),-1.0]])]});}
            var Q56;
            {var subQ4=sQuery(id+"F18.wireOp",EDGE,"E41.top");Q56=makeQuery(id+"F18.imprint","IMPRINT",FACE,{"disambiguationData":[TD([[makeQuery(id+"F18.imprint","IMPRINT",EDGE,{"derivedFrom":subQ4}),1.0]])]});}
            var Q57;
            Q57=makeQuery(id+"F18.imprint","IMPRINT",FACE,{"disambiguationData":[TD([[makeQuery(id+"F18.imprint","IMPRINT",EDGE,{"derivedFrom":sQuery(id+"F18.wireOp",EDGE,"E40.top")}),-1.0]])]});
            var Q58;
            {var subQ0=sQuery(id+"F18.wireOp",EDGE,"E40.bottom");Q58=makeQuery(id+"F18.imprint","IMPRINT",FACE,{"disambiguationData":[TD([[makeQuery(id+"F18.imprint","IMPRINT",EDGE,{"derivedFrom":subQ0}),1.0]])]});}
            var Q59;
            {var subQ0=sQuery(id+"F18.wireOp",EDGE,"E67");Q59=makeQuery(id+"F18.imprint","IMPRINT",FACE,{"disambiguationData":[TD([[makeQuery(id+"F18.imprint","IMPRINT",EDGE,{"derivedFrom":subQ0}),1.0]])]});}
            extrude(context, id + "F28", {"entities" : qUnion([Q0, Q1, Q2, Q3, Q4, Q5, Q6, Q7, Q8, Q9, Q10, Q11, Q12, Q13, Q14, Q15, Q16, Q17, Q18, Q19, Q20, Q21, Q22, Q23, Q24, Q25, Q26, Q27, Q28, Q29, Q30, Q31, Q32, Q33, Q34, Q35, Q36, Q37, Q38, Q39, Q40, Q41, Q42, Q43, Q44, Q45, Q46, Q47, Q48, Q49, Q50, Q51, Q52, Q53, Q54, Q55, Q56, Q57, Q58, Q59]), "operationType" : NewBodyOperationType.REMOVE, "oppositeDirection" : true, "depth" : 6.35 * mm});
        }
        {
            var Q0;
            Q0=makeQuery(id+"F28.boolean.opBoolean","COPY",EDGE,{"derivedFrom":makeQuery(id+"F28.opExtrude","SWEPT_EDGE",EDGE,{"disambiguationData":[OSD([sQuery(id+"F18.wireOp",EDGE,"E40.top"),sQuery(id+"F18.wireOp",EDGE,"E40.right")])]})});
            var Q1;
            Q1=makeQuery(id+"F28.boolean.opBoolean","COPY",EDGE,{"derivedFrom":makeQuery(id+"F28.opExtrude","SWEPT_EDGE",EDGE,{"disambiguationData":[OSD([sQuery(id+"F18.wireOp",EDGE,"E40.top"),sQuery(id+"F18.wireOp",EDGE,"E40.left")])]})});
            var Q2;
            Q2=makeQuery(id+"F28.boolean.opBoolean","COPY",EDGE,{"derivedFrom":makeQuery(id+"F28.opExtrude","SWEPT_EDGE",EDGE,{"disambiguationData":[OSD([sQuery(id+"F18.wireOp",EDGE,"E41.top"),sQuery(id+"F18.wireOp",EDGE,"E41.left")])]})});
            var Q3;
            Q3=makeQuery(id+"F28.boolean.opBoolean","COPY",EDGE,{"derivedFrom":makeQuery(id+"F28.opExtrude","SWEPT_EDGE",EDGE,{"disambiguationData":[OSD([sQuery(id+"F18.wireOp",EDGE,"E41.top"),sQuery(id+"F18.wireOp",EDGE,"E41.right")])]})});
            var Q4;
            Q4=makeQuery(id+"F28.boolean.opBoolean","COPY",EDGE,{"derivedFrom":makeQuery(id+"F28.opExtrude","SWEPT_EDGE",EDGE,{"disambiguationData":[OSD([sQuery(id+"F18.wireOp",EDGE,"E42.top"),sQuery(id+"F18.wireOp",EDGE,"E42.right")])]})});
            var Q5;
            Q5=makeQuery(id+"F28.boolean.opBoolean","COPY",EDGE,{"derivedFrom":makeQuery(id+"F28.opExtrude","SWEPT_EDGE",EDGE,{"disambiguationData":[OSD([sQuery(id+"F18.wireOp",EDGE,"E39.top"),sQuery(id+"F18.wireOp",EDGE,"E39.left")])]})});
            var Q6;
            Q6=makeQuery(id+"F28.boolean.opBoolean","COPY",EDGE,{"derivedFrom":makeQuery(id+"F28.opExtrude","SWEPT_EDGE",EDGE,{"disambiguationData":[OSD([sQuery(id+"F18.wireOp",EDGE,"E39.top"),sQuery(id+"F18.wireOp",EDGE,"E39.right")])]})});
            var Q7;
            Q7=makeQuery(id+"F28.boolean.opBoolean","COPY",EDGE,{"derivedFrom":makeQuery(id+"F28.opExtrude","SWEPT_EDGE",EDGE,{"disambiguationData":[OSD([sQuery(id+"F18.wireOp",EDGE,"E42.top"),sQuery(id+"F18.wireOp",EDGE,"E42.left")])]})});
            fillet(context, id + "F29", {"entities" : qUnion([Q0, Q1, Q2, Q3, Q4, Q5, Q6, Q7]), "radius" : 3.17 * mm, "tangentPropagation" : true, "allowEdgeOverflow" : false});
        }
        {
            var Q0;
            Q0=makeQuery(id+"F1.opExtrude","SWEPT_FACE",FACE,{"disambiguationData":[OSD([sQuery(id+"F0.wireOp",EDGE,"E0.top")])]});
            var sketch = newSketch(context, id + "F30", { "sketchPlane" : qUnion([Q0])});
            skLineSegment(sketch, "E79", {"start": v(-152.4, 85.73) * mm, "end": v(0, 85.73) * mm});
            skLineSegment(sketch, "E80.bottom", {"start": v(6.35, 60.33) * mm, "end": v(-6.35, 60.33) * mm});
            skLineSegment(sketch, "E80.top", {"start": v(6.35, 111.13) * mm, "end": v(-6.35, 111.13) * mm});
            skLineSegment(sketch, "E80.left", {"start": v(9.52, 63.5) * mm, "end": v(9.52, 107.95) * mm});
            skLineSegment(sketch, "E80.right", {"start": v(-9.53, 63.5) * mm, "end": v(-9.53, 107.95) * mm});
            skPoint(sketch, "E80.middle", {"position": v(0, 85.73) * mm});
            skPoint(sketch, "E81.visualSharp", {"position": v(-9.53, 111.13) * mm});
            skArc(sketch, "E81.filletArc", {"start": v(-6.35, 111.13) * mm, "mid": v(-8.6, 110.2) * mm, "end": v(-9.53, 107.95) * mm});
            skPoint(sketch, "E82.visualSharp", {"position": v(9.52, 111.13) * mm});
            skArc(sketch, "E82.filletArc", {"start": v(9.52, 107.95) * mm, "mid": v(8.6, 110.2) * mm, "end": v(6.35, 111.13) * mm});
            skPoint(sketch, "E83.visualSharp", {"position": v(-9.53, 60.33) * mm});
            skArc(sketch, "E83.filletArc", {"start": v(-9.53, 63.5) * mm, "mid": v(-8.6, 61.25) * mm, "end": v(-6.35, 60.33) * mm});
            skPoint(sketch, "E84.visualSharp", {"position": v(9.52, 60.33) * mm});
            skArc(sketch, "E84.filletArc", {"start": v(6.35, 60.33) * mm, "mid": v(8.6, 61.25) * mm, "end": v(9.52, 63.5) * mm});
            skSolve(sketch);
        }
        {
            var Q0;
            Q0 = qSketchRegion(id + "F30", true);
            extrude(context, id + "F31", {"entities" : qUnion([Q0]), "operationType" : NewBodyOperationType.REMOVE, "oppositeDirection" : true, "depth" : 6.35 * mm});
        }
        {
            var Q0;
            {var subQ1=sQuery(id+"F30.wireOp",EDGE,"E80.bottom");Q0=makeQuery(id+"F30.imprint","IMPRINT",FACE,{"disambiguationData":[TD([[makeQuery(id+"F30.imprint","IMPRINT",EDGE,{"derivedFrom":subQ1}),-1.0]])]});}
            var Q1;
            {var subQ1=sQuery(id+"F30.wireOp",EDGE,"E80.top");Q1=makeQuery(id+"F30.imprint","IMPRINT",FACE,{"disambiguationData":[TD([[makeQuery(id+"F30.imprint","IMPRINT",EDGE,{"derivedFrom":subQ1}),1.0]])]});}
            extrude(context, id + "F32", {"entities" : qUnion([Q0, Q1]), "oppositeDirection" : true, "depth" : 6.35 * mm, "hasSecondDirection" : true, "secondDirectionOppositeDirection" : false, "secondDirectionDepth" : 3.05 * mm});
        }
        {
            var Q0;
            Q0=makeQuery(id+"F32.opExtrude","CAP_FACE",FACE,{"disambiguationData":[OSD([sQuery(id+"F30.wireOp",EDGE,"E80.bottom"),sQuery(id+"F30.wireOp",EDGE,"E80.top"),sQuery(id+"F30.wireOp",EDGE,"E80.left"),sQuery(id+"F30.wireOp",EDGE,"E80.right"),sQuery(id+"F30.wireOp",EDGE,"E81.filletArc"),sQuery(id+"F30.wireOp",EDGE,"E82.filletArc"),sQuery(id+"F30.wireOp",EDGE,"E83.filletArc"),sQuery(id+"F30.wireOp",EDGE,"E84.filletArc")])],"isStart":true});
            var sketch = newSketch(context, id + "F33", { "sketchPlane" : qUnion([Q0])});
            skLineSegment(sketch, "E85", {"start": v(0, 111.13) * mm, "end": v(0, 98.43) * mm});
            skCircle(sketch, "E86", {"center": v(0, 98.43) * mm, "radius": 6.35 * mm});
            skLineSegment(sketch, "E87", {"start": v(0, 60.33) * mm, "end": v(0, 73.03) * mm});
            skPoint(sketch, "E87.endSnap0", {"position": v(0, 60.33) * mm});
            skCircle(sketch, "E88", {"center": v(0, 73.03) * mm, "radius": 6.35 * mm});
            skLineSegment(sketch, "E89", {"start": v(-6.35, 73.03) * mm, "end": v(-6.35, 98.43) * mm});
            skLineSegment(sketch, "E90", {"start": v(-6.35, 98.43) * mm, "end": v(6.35, 98.43) * mm});
            skLineSegment(sketch, "E91", {"start": v(6.35, 98.43) * mm, "end": v(6.35, 73.03) * mm});
            skLineSegment(sketch, "E92", {"start": v(0, 111.13) * mm, "end": v(0, 85.73) * mm});
            skLineSegment(sketch, "E93", {"start": v(0, 85.73) * mm, "end": v(-9.53, 85.73) * mm});
            skLineSegment(sketch, "E94", {"start": v(-9.53, 85.73) * mm, "end": v(9.52, 85.73) * mm});
            skSolve(sketch);
        }
        {
            var Q0;
            {var subQ1=sQuery(id+"F33.wireOp",EDGE,"E86");var subQ3=sQuery(id+"F33.wireOp",EDGE,"E92");var subQ4=makeQuery(id+"F33.imprint","INTERSECT",VERTEX,{"disambiguationData":[OD(0.0)],"derivedFrom":[subQ1,subQ3]});Q0=makeQuery(id+"F33.imprint","IMPRINT",FACE,{"disambiguationData":[TD([[makeQuery(id+"F33.imprint","IMPRINT",EDGE,{"disambiguationData":[TD([[subQ4,-1.0]])],"derivedFrom":subQ3}),-1.0]])]});}
            var Q1;
            {var subQ1=sQuery(id+"F33.wireOp",EDGE,"E86");var subQ3=sQuery(id+"F33.wireOp",EDGE,"E92");var subQ4=makeQuery(id+"F33.imprint","INTERSECT",VERTEX,{"disambiguationData":[OD(0.0)],"derivedFrom":[subQ1,subQ3]});Q1=makeQuery(id+"F33.imprint","IMPRINT",FACE,{"disambiguationData":[TD([[makeQuery(id+"F33.imprint","IMPRINT",EDGE,{"disambiguationData":[TD([[subQ4,-1.0]])],"derivedFrom":subQ3}),1.0]])]});}
            var Q2;
            {var subQ1=sQuery(id+"F33.wireOp",EDGE,"E86");var subQ3=sQuery(id+"F33.wireOp",EDGE,"E92");var subQ4=makeQuery(id+"F33.imprint","INTERSECT",VERTEX,{"disambiguationData":[OD(1.0)],"derivedFrom":[subQ1,subQ3]});Q2=makeQuery(id+"F33.imprint","IMPRINT",FACE,{"disambiguationData":[TD([[makeQuery(id+"F33.imprint","IMPRINT",EDGE,{"disambiguationData":[TD([[subQ4,1.0]])],"derivedFrom":subQ3}),-1.0]])]});}
            var Q3;
            {var subQ1=sQuery(id+"F33.wireOp",EDGE,"E86");var subQ3=sQuery(id+"F33.wireOp",EDGE,"E92");var subQ4=makeQuery(id+"F33.imprint","INTERSECT",VERTEX,{"disambiguationData":[OD(1.0)],"derivedFrom":[subQ1,subQ3]});Q3=makeQuery(id+"F33.imprint","IMPRINT",FACE,{"disambiguationData":[TD([[makeQuery(id+"F33.imprint","IMPRINT",EDGE,{"disambiguationData":[TD([[subQ4,1.0]])],"derivedFrom":subQ3}),1.0]])]});}
            extrude(context, id + "F34", {"entities" : qUnion([Q0, Q1, Q2, Q3]), "operationType" : NewBodyOperationType.ADD, "depth" : 2.16 * mm});
        }
        {
            var Q0;
            {var subQ11=makeQuery(id+"F32.opExtrude","CAP_EDGE",EDGE,{"disambiguationData":[OSD([sQuery(id+"F30.wireOp",EDGE,"E84.filletArc")])],"isStart":true});Q0=makeQuery(id+"F33.imprint","IMPRINT",FACE,{"disambiguationData":[TD([[makeQuery(id+"F33.imprint","IMPRINT",EDGE,{"derivedFrom":subQ11}),1.0]])]});}
            var Q1;
            {var subQ11=makeQuery(id+"F32.opExtrude","CAP_EDGE",EDGE,{"disambiguationData":[OSD([sQuery(id+"F30.wireOp",EDGE,"E83.filletArc")])],"isStart":true});Q1=makeQuery(id+"F33.imprint","IMPRINT",FACE,{"disambiguationData":[TD([[makeQuery(id+"F33.imprint","IMPRINT",EDGE,{"derivedFrom":subQ11}),1.0]])]});}
            extrude(context, id + "F35", {"entities" : qUnion([Q0, Q1]), "operationType" : NewBodyOperationType.REMOVE, "oppositeDirection" : true, "depth" : 25.4 * mm});
        }
        {
            var Q0;
            Q0=makeQuery(id+"F32.opExtrude","CAP_FACE",FACE,{"disambiguationData":[OSD([sQuery(id+"F30.wireOp",EDGE,"E80.bottom"),sQuery(id+"F30.wireOp",EDGE,"E80.top"),sQuery(id+"F30.wireOp",EDGE,"E80.left"),sQuery(id+"F30.wireOp",EDGE,"E80.right"),sQuery(id+"F30.wireOp",EDGE,"E81.filletArc"),sQuery(id+"F30.wireOp",EDGE,"E82.filletArc"),sQuery(id+"F30.wireOp",EDGE,"E83.filletArc"),sQuery(id+"F30.wireOp",EDGE,"E84.filletArc")])],"isStart":false});
            var sketch = newSketch(context, id + "F36", { "sketchPlane" : qUnion([Q0])});
            skLineSegment(sketch, "E95", {"start": v(-6.35, 85.73) * mm, "end": v(6.35, 85.73) * mm});
            skSolve(sketch);
        }
        {
            var Q0;
            Q0=makeQuery(id+"F36.imprint","IMPRINT",FACE,{"disambiguationData":[TD([[makeQuery(id+"F36.imprint","IMPRINT",EDGE,{"derivedFrom":sQuery(id+"F36.wireOp",EDGE,"E95")}),-1.0]])]});
            extrude(context, id + "F37", {"entities" : qUnion([Q0]), "operationType" : NewBodyOperationType.REMOVE, "oppositeDirection" : true, "depth" : 5.08 * mm});
        }
        {
            var Q0;
            Q0=makeQuery(id+"F37.boolean.opBoolean","COPY",FACE,{"derivedFrom":makeQuery(id+"F37.opExtrude","CAP_FACE",FACE,{"disambiguationData":[OSD([sQuery(id+"F30.wireOp",EDGE,"E80.bottom"),sQuery(id+"F30.wireOp",EDGE,"E80.top"),sQuery(id+"F30.wireOp",EDGE,"E80.left"),sQuery(id+"F30.wireOp",EDGE,"E80.right"),sQuery(id+"F30.wireOp",EDGE,"E81.filletArc"),sQuery(id+"F30.wireOp",EDGE,"E82.filletArc"),sQuery(id+"F30.wireOp",EDGE,"E83.filletArc"),sQuery(id+"F30.wireOp",EDGE,"E84.filletArc"),sQuery(id+"F33.wireOp",EDGE,"E88"),sQuery(id+"F33.wireOp",EDGE,"E89"),sQuery(id+"F33.wireOp",EDGE,"E91"),sQuery(id+"F36.wireOp",EDGE,"E95")])],"isStart":false})});
            var sketch = newSketch(context, id + "F38", { "sketchPlane" : qUnion([Q0])});
            skCircle(sketch, "E96", {"center": v(0, 73.03) * mm, "radius": 6.35 * mm});
            skSolve(sketch);
        }
        {
            var Q0;
            {var subQ0=sQuery(id+"F38.wireOp",EDGE,"E96");Q0=makeQuery(id+"F38.imprint","IMPRINT",FACE,{"disambiguationData":[TD([[makeQuery(id+"F38.imprint","IMPRINT",EDGE,{"disambiguationData":[OD(0.0)],"derivedFrom":subQ0}),1.0]])]});}
            extrude(context, id + "F39", {"entities" : qUnion([Q0]), "operationType" : NewBodyOperationType.ADD, "depth" : 2.54 * mm});
        }
        {
            var Q0;
            Q0=makeQuery(id+"F35.boolean.opBoolean","COPY",FACE,{"derivedFrom":makeQuery(id+"F35.opExtrude","SWEPT_FACE",FACE,{"disambiguationData":[OSD([sQuery(id+"F33.wireOp",EDGE,"E91")])]})});
            var sketch = newSketch(context, id + "F40", { "sketchPlane" : qUnion([Q0])});
            skLineSegment(sketch, "E97", {"start": v(-117.35, 73.03) * mm, "end": v(-117.35, 51.25) * mm});
            skLineSegment(sketch, "E98", {"start": v(-117.35, 73.03) * mm, "end": v(-110.5, 73.03) * mm});
            skLineSegment(sketch, "E99", {"start": v(-117.35, 73.03) * mm, "end": v(-117.35, 66.17) * mm});
            skLineSegment(sketch, "E100", {"start": v(-117.35, 66.17) * mm, "end": v(-110.5, 73.03) * mm});
            skLineSegment(sketch, "E101", {"start": v(-117.35, 66.17) * mm, "end": v(-117.35, 65.53) * mm});
            skLineSegment(sketch, "E102", {"start": v(-117.35, 65.53) * mm, "end": v(-114.43, 68.45) * mm});
            skLineSegment(sketch, "E103", {"start": v(-114.43, 68.45) * mm, "end": v(-106.8, 76.08) * mm});
            skLineSegment(sketch, "E104", {"start": v(-106.8, 76.08) * mm, "end": v(-106.8, 65.53) * mm});
            skLineSegment(sketch, "E105", {"start": v(-106.8, 65.53) * mm, "end": v(-117.35, 65.53) * mm});
            skSolve(sketch);
        }
        {
            var Q0;
            Q0=makeQuery(id+"F40.imprint","IMPRINT",FACE,{"disambiguationData":[TD([[makeQuery(id+"F40.imprint","IMPRINT",EDGE,{"derivedFrom":sQuery(id+"F40.wireOp",EDGE,"E102")}),-1.0]])]});
            extrude(context, id + "F41", {"entities" : qUnion([Q0]), "oppositeDirection" : true, "depth" : 25.4 * mm});
        }
        {
            var Q0;
            Q0=makeQuery(id+"F41.opExtrude","SWEPT_BODY",BODY,{"disambiguationData":[OSD([sQuery(id+"F40.wireOp",EDGE,"E102"),sQuery(id+"F40.wireOp",EDGE,"E103"),sQuery(id+"F40.wireOp",EDGE,"E104"),sQuery(id+"F40.wireOp",EDGE,"E105")])]});
            var Q1;
            Q1=makeQuery(id+"F32.opExtrude","SWEPT_BODY",BODY,{"disambiguationData":[OSD([sQuery(id+"F30.wireOp",EDGE,"E80.bottom"),sQuery(id+"F30.wireOp",EDGE,"E80.top"),sQuery(id+"F30.wireOp",EDGE,"E80.left"),sQuery(id+"F30.wireOp",EDGE,"E80.right"),sQuery(id+"F30.wireOp",EDGE,"E81.filletArc"),sQuery(id+"F30.wireOp",EDGE,"E82.filletArc"),sQuery(id+"F30.wireOp",EDGE,"E83.filletArc"),sQuery(id+"F30.wireOp",EDGE,"E84.filletArc")])]});
            booleanBodies(context, id + "F42", {"operationType" : BooleanOperationType.SUBTRACTION, "tools" : qUnion([Q0]), "targets" : qUnion([Q1])});
        }
        {
            var Q0;
            Q0=makeQuery(id+"F1.opExtrude","SWEPT_FACE",FACE,{"disambiguationData":[OSD([sQuery(id+"F0.wireOp",EDGE,"E0.top")])]});
            var sketch = newSketch(context, id + "F43", { "sketchPlane" : qUnion([Q0])});
            skLineSegment(sketch, "E106.bottom", {"start": v(-9.53, 85.73) * mm, "end": v(9.52, 85.73) * mm});
            skLineSegment(sketch, "E106.top", {"start": v(-6.35, 60.33) * mm, "end": v(6.35, 60.33) * mm});
            skLineSegment(sketch, "E106.left", {"start": v(-9.53, 85.73) * mm, "end": v(-9.53, 63.5) * mm});
            skLineSegment(sketch, "E106.right", {"start": v(9.52, 85.73) * mm, "end": v(9.52, 63.5) * mm});
            skPoint(sketch, "E107.visualSharp", {"position": v(9.52, 60.33) * mm});
            skArc(sketch, "E107.filletArc", {"start": v(6.35, 60.33) * mm, "mid": v(8.6, 61.25) * mm, "end": v(9.52, 63.5) * mm});
            skPoint(sketch, "E108.visualSharp", {"position": v(-9.53, 60.33) * mm});
            skArc(sketch, "E108.filletArc", {"start": v(-9.53, 63.5) * mm, "mid": v(-8.6, 61.25) * mm, "end": v(-6.35, 60.33) * mm});
            skSolve(sketch);
        }
        {
            var Q0;
            Q0 = qSketchRegion(id + "F43", true);
            extrude(context, id + "F44", {"entities" : qUnion([Q0]), "oppositeDirection" : true, "depth" : 6.35 * mm, "hasSecondDirection" : true, "secondDirectionOppositeDirection" : false, "secondDirectionDepth" : 3.05 * mm});
        }
        {
            var Q0;
            Q0=makeQuery(id+"F32.opExtrude","SWEPT_BODY",BODY,{"disambiguationData":[OSD([sQuery(id+"F30.wireOp",EDGE,"E80.bottom"),sQuery(id+"F30.wireOp",EDGE,"E80.top"),sQuery(id+"F30.wireOp",EDGE,"E80.left"),sQuery(id+"F30.wireOp",EDGE,"E80.right"),sQuery(id+"F30.wireOp",EDGE,"E81.filletArc"),sQuery(id+"F30.wireOp",EDGE,"E82.filletArc"),sQuery(id+"F30.wireOp",EDGE,"E83.filletArc"),sQuery(id+"F30.wireOp",EDGE,"E84.filletArc")])]});
            var Q1;
            Q1=makeQuery(id+"F44.opExtrude","SWEPT_BODY",BODY,{"disambiguationData":[OSD([sQuery(id+"F43.wireOp",EDGE,"E106.bottom"),sQuery(id+"F43.wireOp",EDGE,"E106.top"),sQuery(id+"F43.wireOp",EDGE,"E106.left"),sQuery(id+"F43.wireOp",EDGE,"E106.right"),sQuery(id+"F43.wireOp",EDGE,"E107.filletArc"),sQuery(id+"F43.wireOp",EDGE,"E108.filletArc")])]});
            booleanBodies(context, id + "F45", {"operationType" : BooleanOperationType.SUBTRACTION, "tools" : qUnion([Q0]), "targets" : qUnion([Q1]), "keepTools" : true});
        }
        {
            var Q0;
            Q0=makeQuery(id+"F32.opExtrude","CAP_EDGE",EDGE,{"disambiguationData":[OSD([sQuery(id+"F30.wireOp",EDGE,"E80.right")])],"isStart":true});
            var Q1;
            Q1=makeQuery(id+"F32.opExtrude","CAP_EDGE",EDGE,{"disambiguationData":[OSD([sQuery(id+"F30.wireOp",EDGE,"E81.filletArc")])],"isStart":true});
            var Q2;
            Q2=makeQuery(id+"F32.opExtrude","CAP_EDGE",EDGE,{"disambiguationData":[OSD([sQuery(id+"F30.wireOp",EDGE,"E80.top")])],"isStart":true});
            var Q3;
            Q3=makeQuery(id+"F32.opExtrude","CAP_EDGE",EDGE,{"disambiguationData":[OSD([sQuery(id+"F30.wireOp",EDGE,"E82.filletArc")])],"isStart":true});
            var Q4;
            Q4=makeQuery(id+"F44.opExtrude","CAP_EDGE",EDGE,{"disambiguationData":[OSD([sQuery(id+"F43.wireOp",EDGE,"E106.left")])],"isStart":true});
            chamfer(context, id + "F46", {"entities" : qUnion([Q0, Q1, Q2, Q3, Q4]), "width" : 1.52 * mm, "tangentPropagation" : true});
        }
        {
            var Q0;
            Q0=makeQuery(id+"F16.opExtrude","CAP_FACE",FACE,{"disambiguationData":[OSD([sQuery(id+"F11.wireOp",EDGE,"E31.bottom"),sQuery(id+"F11.wireOp",EDGE,"E31.top"),sQuery(id+"F11.wireOp",EDGE,"E31.left"),sQuery(id+"F11.wireOp",EDGE,"E31.right"),sQuery(id+"F11.wireOp",EDGE,"E32.bottom"),sQuery(id+"F11.wireOp",EDGE,"E32.left"),sQuery(id+"F11.wireOp",EDGE,"E33.bottom"),sQuery(id+"F11.wireOp",EDGE,"E33.left")])],"isStart":true});
            var sketch = newSketch(context, id + "F47", { "sketchPlane" : qUnion([Q0])});
            skCircle(sketch, "E109", {"center": v(0, 0) * mm, "radius": 23.5 * mm});
            skSolve(sketch);
        }
        {
            var Q0;
            Q0 = qSketchRegion(id + "F47", true);
            extrude(context, id + "F48", {"entities" : qUnion([Q0]), "depth" : 10.16 * mm});
        }
        {
            var Q0;
            Q0=makeQuery(id+"F48.opExtrude","CAP_FACE",FACE,{"disambiguationData":[OSD([sQuery(id+"F47.wireOp",EDGE,"E109")])],"isStart":false});
            var sketch = newSketch(context, id + "F49", { "sketchPlane" : qUnion([Q0])});
            skLineSegment(sketch, "E110.bottom", {"start": v(15.88, 7) * mm, "end": v(-15.88, 7) * mm});
            skLineSegment(sketch, "E110.top", {"start": v(15.88, -7) * mm, "end": v(-15.88, -7) * mm});
            skLineSegment(sketch, "E110.left", {"start": v(15.88, 7) * mm, "end": v(15.88, -7) * mm});
            skLineSegment(sketch, "E110.right", {"start": v(-15.88, 7) * mm, "end": v(-15.88, -7) * mm});
            skPoint(sketch, "E110.middle", {"position": v(0, 0) * mm});
            skSolve(sketch);
        }
        {
            var Q0;
            Q0=makeQuery(id+"F49.imprint","IMPRINT",FACE,{"disambiguationData":[TD([[makeQuery(id+"F49.imprint","IMPRINT",EDGE,{"derivedFrom":sQuery(id+"F49.wireOp",EDGE,"E110.bottom")}),-1.0]])]});
            extrude(context, id + "F50", {"entities" : qUnion([Q0]), "depth" : 2.54 * mm});
        }
        {
            var Q0;
            Q0=makeQuery(id+"F49.imprint","IMPRINT",FACE,{"disambiguationData":[TD([[makeQuery(id+"F49.imprint","IMPRINT",EDGE,{"derivedFrom":sQuery(id+"F49.wireOp",EDGE,"E110.bottom")}),1.0]])]});
            extrude(context, id + "F51", {"entities" : qUnion([Q0]), "depth" : 2.54 * mm});
        }
    });
